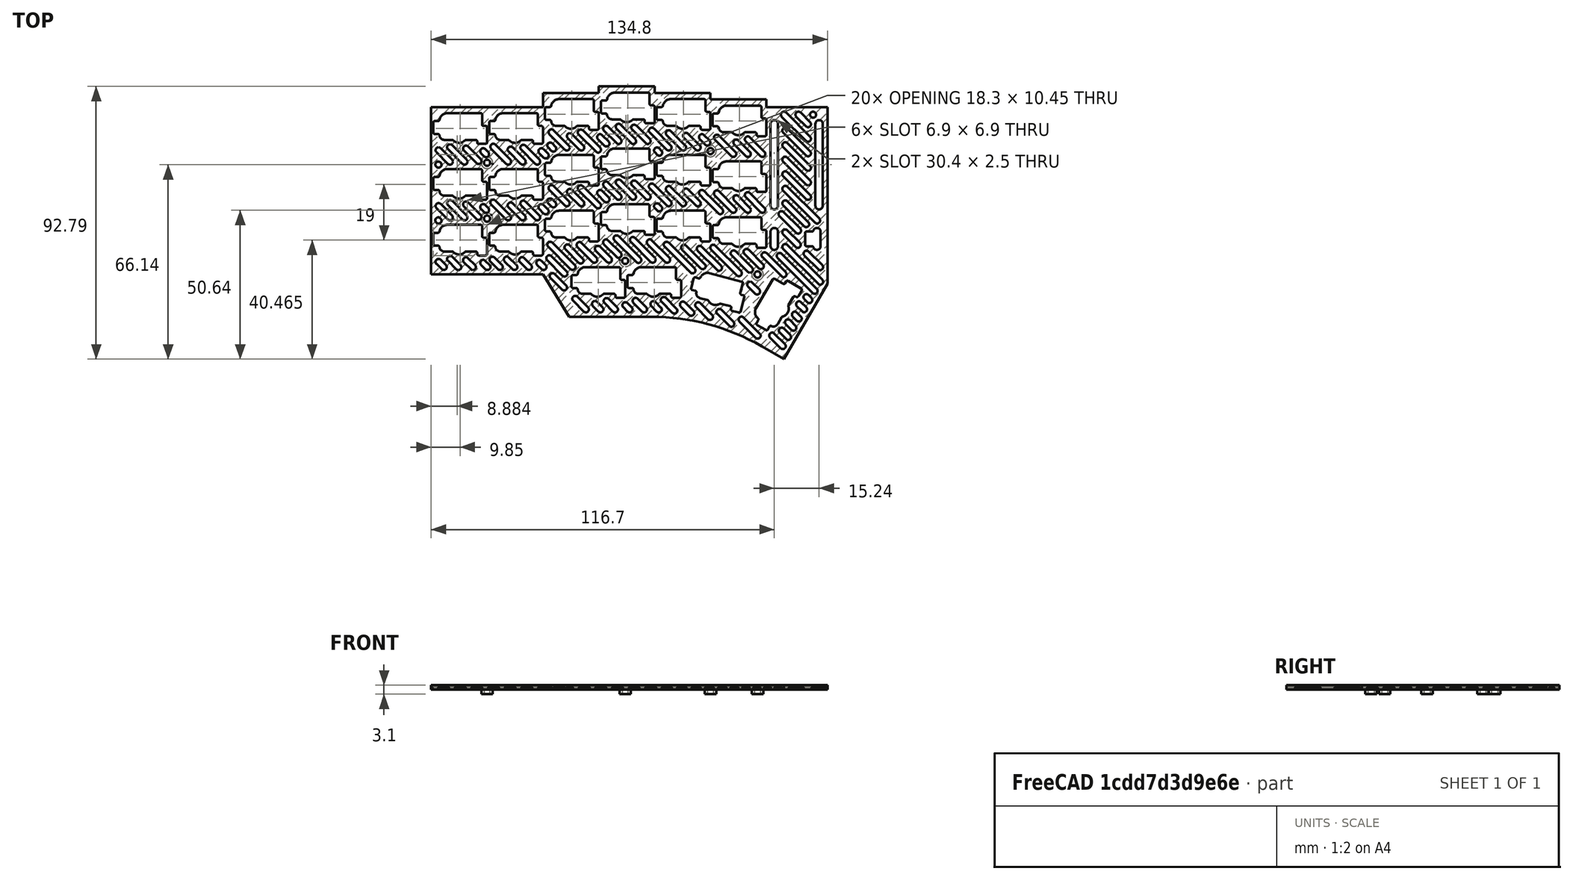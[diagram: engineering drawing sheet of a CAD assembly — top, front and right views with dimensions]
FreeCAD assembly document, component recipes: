
FREECAD ASSEMBLY — COMPONENT RECIPES ("key-v3")

This assembly document has 4 components, labeled P0..P3 below (a component is one placed body or linked part). 4 of them carry a construction recipe — the FreeCAD feature program that regenerates the part from scratch, quoted from this document or its linked companion documents; the rest are supplied as boundary geometry only. No exploded tour is included for this assembly.
COMPONENT P0 — recipe-attached ("base body", modeled in this document).
Construction recipe (the document's own serialized feature program — sketch geometry with constraints, then the solid features built on it; lengths are millimeters unless a unit is written):

FEATURE [Sketcher::SketchObject] Sketch001  label="pcb contour"
  AttachmentSupport = -> [XY_Plane]
  FullyConstrained = true
  MapMode = 5
  expr: Constraints[36] = 19 * 3
  sketch-geometry (39):
    g0: LineSegment StartX=-9.5 StartY=9.5 StartZ=0 EndX=28.5 EndY=9.5 EndZ=0
    g1: LineSegment StartX=28.5 StartY=9.5 StartZ=0 EndX=28.5 EndY=14.3 EndZ=0
    g2: LineSegment StartX=28.5 StartY=14.3 StartZ=0 EndX=47.5 EndY=14.3 EndZ=0
    g3: LineSegment StartX=47.5 StartY=14.3 StartZ=0 EndX=47.5 EndY=16.5 EndZ=0
    g4: LineSegment StartX=47.5 StartY=16.5 StartZ=0 EndX=66.5 EndY=16.5 EndZ=0
    g5: LineSegment StartX=66.5 StartY=16.5 StartZ=0 EndX=66.5 EndY=14.3 EndZ=0
    g6: LineSegment StartX=66.5 StartY=14.3 StartZ=0 EndX=85.5 EndY=14.3 EndZ=0
    g7: LineSegment StartX=85.5 StartY=14.3 StartZ=0 EndX=85.5 EndY=12.1 EndZ=0
    g8: LineSegment StartX=85.5 StartY=12.1 StartZ=0 EndX=104.5 EndY=12.1 EndZ=0
    g9: LineSegment StartX=104.5 StartY=12.1 StartZ=0 EndX=104.5 EndY=9.4 EndZ=0
    g10: LineSegment StartX=104.5 StartY=9.4 StartZ=0 EndX=125.3 EndY=9.4 EndZ=0
    g11: LineSegment StartX=-9.5 StartY=9.5 StartZ=0 EndX=-9.5 EndY=-47.5 EndZ=0
    g12: LineSegment StartX=-9.5 StartY=-47.5 StartZ=0 EndX=28.5 EndY=-47.5 EndZ=0
    g13: LineSegment StartX=28.5 StartY=-47.5 StartZ=0 EndX=37.45 EndY=-61.9 EndZ=0
    g14: LineSegment StartX=37.45 StartY=-61.9 StartZ=0 EndX=56.45 EndY=-61.9 EndZ=0
    g15: LineSegment StartX=56.45 StartY=-61.9 StartZ=0 EndX=56.45 EndY=-42.9 EndZ=0
    g16: LineSegment StartX=56.45 StartY=-42.9 StartZ=0 EndX=37.45 EndY=-42.9 EndZ=0
    g17: LineSegment StartX=37.45 StartY=-42.9 StartZ=0 EndX=37.45 EndY=-61.9 EndZ=0
    g18: LineSegment StartX=56.45 StartY=-61.9 StartZ=0 EndX=75.45 EndY=-61.9 EndZ=0
    g19: LineSegment StartX=75.45 StartY=-61.9 StartZ=0 EndX=75.45 EndY=-42.9 EndZ=0
    g20: LineSegment StartX=75.45 StartY=-42.9 StartZ=0 EndX=56.45 EndY=-42.9 EndZ=0
    g21: LineSegment StartX=56.45 StartY=-42.9 StartZ=0 EndX=56.45 EndY=-61.9 EndZ=0
    g22: GeomPoint X=65.95 Y=-52.4 Z=0
    g23: LineSegment StartX=110.452 StartY=-76.2909 StartZ=0 EndX=93.9978 EndY=-66.7909 EndZ=0
    g24: LineSegment StartX=93.9978 StartY=-66.7909 StartZ=0 EndX=108.248 EndY=-42.1091 EndZ=0
    g25: LineSegment StartX=108.248 StartY=-42.1091 StartZ=0 EndX=124.702 EndY=-51.6091 EndZ=0
    g26: LineSegment StartX=124.702 StartY=-51.6091 StartZ=0 EndX=110.452 EndY=-76.2909 EndZ=0
    g27: GeomPoint X=109.35 Y=-59.2 Z=0
    g28: LineSegment StartX=75.5149 StartY=-61.9175 StartZ=0 EndX=80.4325 EndY=-43.5649 EndZ=0
    g29: LineSegment StartX=80.4325 StartY=-43.5649 StartZ=0 EndX=98.7851 EndY=-48.4825 EndZ=0
    g30: LineSegment StartX=98.7851 StartY=-48.4825 StartZ=0 EndX=93.8675 EndY=-66.8351 EndZ=0
    g31: LineSegment StartX=93.8675 StartY=-66.8351 StartZ=0 EndX=75.5149 EndY=-61.9175 EndZ=0
    g32: GeomPoint X=87.15 Y=-55.2 Z=0
    g33: LineSegment StartX=37.45 StartY=-61.9 StartZ=0 EndX=65.4303 EndY=-61.9 EndZ=0
    g34: LineSegment StartX=110.452 StartY=-76.2909 StartZ=0 EndX=102.93 EndY=-71.9481 EndZ=0
    g35: LineSegment StartX=125.3 StartY=9.4 StartZ=0 EndX=125.3 EndY=-50.5738 EndZ=0
    g36: LineSegment StartX=110.452 StartY=-76.2909 StartZ=0 EndX=125.3 EndY=-50.5738 EndZ=0
    g37: ArcOfCircle CenterX=65.4303 CenterY=-136.9 CenterZ=0 NormalX=0 NormalY=0 NormalZ=1 AngleXU=0 Radius=75 StartAngle=1.0472 EndAngle=1.5708
    g38: GeomPoint X=85.5265 Y=-61.9 Z=0
  constraints (105):
    c: Horizontal(g0)
    c: Coincident(g1,g0)
    c: Vertical(g1)
    c: Coincident(g2,g1)
    c: Horizontal(g2)
    c: Coincident(g3,g2)
    c: Vertical(g3)
    c: Coincident(g4,g3)
    c: Horizontal(g4)
    c: Coincident(g5,g4)
    c: Vertical(g5)
    c: Coincident(g6,g5)
    c: Horizontal(g6)
    c: Coincident(g7,g6)
    c: Vertical(g7)
    c: Coincident(g8,g7)
    c: Horizontal(g8)
    c: Coincident(g9,g8)
    c: Vertical(g9)
    c: Coincident(g10,g9)
    c: Horizontal(g10)
    c: DistanceX(g0,g-1) = 9.5
    c: Distance(g-1,g0) = 9.5
    c: DistanceX(g0,g0) = 38
    c: DistanceX(g2,g2) = 19
    c: Equal(g4,g2)
    c: Equal(g2,g6)
    c: Equal(g6,g8)
    c: DistanceY(g1,g1) = 4.8
    c: DistanceY(g3,g3) = 2.2
    c: DistanceY(g5,g5) = 2.2
    c: DistanceY(g7,g7) = 2.2
    c: DistanceY(g9,g9) = 2.7
    c: DistanceX(g10,g10) = 20.8
    c: Coincident(g11,g0)
    c: Vertical(g11)
    c: DistanceY(g11,g11) = 57
    c: Coincident(g12,g11)
    c: Horizontal(g12)
    c: DistanceX(g12,g12) = 38
    c: Coincident(g13,g12)
    c: DistanceX(g12,g13) = 8.95
    c: DistanceY(g13,g12) = 14.4
    c: Coincident(g14,g15)
    c: Coincident(g15,g16)
    c: Coincident(g16,g17)
    c: Coincident(g17,g14)
    c: Horizontal(g14)
    c: Horizontal(g16)
    c: Vertical(g15)
    c: Vertical(g17)
    c: Coincident(g14,g13)
    c: Equal(g17,g16)
    c: DistanceX(g16,g16) = 19
    c: Coincident(g18,g19)
    c: Coincident(g19,g20)
    c: Coincident(g20,g21)
    c: Coincident(g21,g18)
    c: Horizontal(g18)
    c: Horizontal(g20)
    c: Vertical(g19)
    c: Vertical(g21)
    c: Coincident(g18,g14)
    c: Equal(g20,g19)
    c: Equal(g19,g16)
    c: Symmetric(g14,g19,g22)
    c: Coincident(g24,g23)
    c: Coincident(g25,g24)
    c: Coincident(g26,g25)
    c: Coincident(g26,g23)
    c: Parallel(g25,g23)
    c: Parallel(g24,g26)
    c: Perpendicular(g25,g24)
    c: Equal(g23,g19)
    c: Symmetric(g25,g23,g27)
    c: Coincident(g29,g28)
    c: Coincident(g30,g29)
    c: Coincident(g31,g30)
    c: Coincident(g31,g28)
    c: Parallel(g30,g28)
    c: Parallel(g29,g31)
    c: Perpendicular(g30,g29)
    c: Equal(g29,g28)
    c: Symmetric(g30,g28,g32)
    c: Angle(g31,g18) = 0.261799
    c: Angle(g18,g26) = 1.0472
    c: DistanceX(g22,g32) = 21.2
    c: DistanceY(g32,g22) = 2.8
    c: Equal(g28,g19)
    c: DistanceX(g32,g27) = 22.2
    c: DistanceY(g27,g32) = 4
    c: Distance(g26,g26) = 28.5
    c: Coincident(g33,g13)
    c: Horizontal(g33)
    c: Tangent(g34,g23) = -1.5708
    c: Coincident(g35,g10)
    c: Vertical(g35)
    c: Coincident(g36,g23)
    c: Tangent(g26,g36)
    c: Coincident(g36,g35)
    c: PointOnObject(g38,g34)
    c: PointOnObject(g38,g33)
    c: Tangent(g34,g37) = -1.5708
    c: Tangent(g33,g37) = 1.5708
    c: Radius(g37) = 75
FEATURE [PartDesign::Pad] Pad  label="base"
  Direction = (0,0,1)
  Length = 1.5
  Length2 = 10
  Profile = -> Sketch001
  ReferenceAxis = -> Sketch001 [N_Axis]
  Suppressed = false
  Type = 0
  expr: Length = <<constants>>.base_normal
FEATURE [PartDesign::Body] Body  label="base body"
  Group = -> [Sketch001,Pad]
  Origin = -> Origin
  Tip = -> Pad
COMPONENT P1 — recipe-attached ("Body003", modeled in this document).
Construction recipe (the document's own serialized feature program — sketch geometry with constraints, then the solid features built on it; lengths are millimeters unless a unit is written):

FEATURE [PartDesign::FeatureBase] BaseFeature
  BaseFeature = -> Cut002
  Suppressed = false
FEATURE [PartDesign::Plane] DatumPlane
  AttachmentSupport = -> [BaseFeature,Z_Axis003]
  Length = 196.764
  MapMode = 13
  Placement = pos=(-6.33333,6.33333,0.5) rot=(0.281085,0.678598,0.678598;2.59356rad)
  ResizeMode = 0
  Width = 68.8627
FEATURE [Sketcher::SketchObject] Sketch003
  AttachmentSupport = -> [DatumPlane]
  ExternalGeometry = -> [BaseFeature]
  FullyConstrained = true
  MapMode = 5
  Placement = pos=(-6.33333,6.33333,0.5) rot=(0.281085,0.678598,0.678598;2.59356rad)
  expr: Constraints[6] = <<constants>>.slot_height
  expr: Constraints[9] = <<constants>>.base_thin
  sketch-geometry (4):
    g0: ArcOfCircle CenterX=2.17834 CenterY=0.1 CenterZ=0 NormalX=0 NormalY=0 NormalZ=1 AngleXU=0 Radius=0.3 StartAngle=4.71239 EndAngle=7.85398
    g1: ArcOfCircle CenterX=0.178343 CenterY=0.1 CenterZ=0 NormalX=0 NormalY=0 NormalZ=1 AngleXU=0 Radius=0.3 StartAngle=1.5708 EndAngle=4.71239
    g2: LineSegment StartX=2.17834 StartY=-0.2 StartZ=0 EndX=0.178343 EndY=-0.2 EndZ=0
    g3: LineSegment StartX=2.17834 StartY=0.4 StartZ=0 EndX=0.178343 EndY=0.4 EndZ=0
  constraints (10):
    c: Tangent(g0,g2) = 1.5708
    c: Tangent(g0,g3) = -1.5708
    c: Tangent(g1,g2) = 1.5708
    c: Tangent(g1,g3) = -1.5708
    c: Equal(g0,g1)
    c: Horizontal(g2)
    c: Distance(g3,g2) = 0.6
    c: DistanceX(g1,g0) = 2
    c: Distance(g0,g-4) = 2
    c: Distance(g-5,g2) = 0.3
FEATURE [PartDesign::Pocket] Pocket
  BaseFeature = -> BaseFeature
  Direction = (-0.707107,-0.707107,0)
  Length = 5
  Length2 = 5
  Midplane = true
  Profile = -> Sketch003
  ReferenceAxis = -> Sketch003 [N_Axis]
  Suppressed = false
  Type = 1
FEATURE [PartDesign::LinearPattern] LinearPattern
  BaseFeature = -> Pocket
  Direction = -> Sketch003 [H_Axis]
  Length = 156
  Mode = 1
  Occurrences = 40
  Offset = 4
  Originals = -> [Pocket]
  Reversed = true
  Suppressed = false
FEATURE [Sketcher::SketchObject] Sketch004
  AttachmentSupport = -> [LinearPattern]
  FullyConstrained = true
  MapMode = 5
  Placement = pos=(0,0,0) rot=(1,0,0;3.14159rad)
  expr: Constraints[5] = 9.5 + 19
  sketch-geometry (5):
    g0: Circle CenterX=9.5 CenterY=9.5 CenterZ=0 NormalX=0 NormalY=0 NormalZ=1 AngleXU=0 Radius=1.95
    g1: Circle CenterX=9.5 CenterY=28.5 CenterZ=0 NormalX=0 NormalY=0 NormalZ=1 AngleXU=0 Radius=1.95
    g2: Circle CenterX=56.5 CenterY=42.9 CenterZ=0 NormalX=0 NormalY=0 NormalZ=1 AngleXU=0 Radius=1.95
    g3: Circle CenterX=85.5 CenterY=5.5 CenterZ=0 NormalX=0 NormalY=0 NormalZ=1 AngleXU=0 Radius=1.95
    g4: Circle CenterX=101.5 CenterY=47.5 CenterZ=0 NormalX=0 NormalY=0 NormalZ=1 AngleXU=0 Radius=1.95
  constraints (15):
    c: Diameter(g0) = 3.9
    c: DistanceY(g-1,g0) = 9.5
    c: DistanceX(g-1,g0) = 9.5
    c: Equal(g1,g0)
    c: Distance(g1,g-2) = 9.5
    c: Distance(g1,g-1) = 28.5
    c: DistanceX(g-1,g2) = 56.5
    c: DistanceY(g-1,g2) = 42.9
    c: Equal(g2,g3)
    c: Equal(g3,g1)
    c: DistanceX(g-1,g3) = 85.5
    c: DistanceY(g-1,g3) = 5.5
    c: DistanceX(g-1,g4) = 101.5
    c: DistanceY(g-1,g4) = 47.5
    c: Equal(g4,g0)
FEATURE [PartDesign::Pad] Pad002
  BaseFeature = -> LinearPattern
  Direction = (0,0,-1)
  Length = 1.6
  Length2 = 10
  Profile = -> Sketch004
  ReferenceAxis = -> Sketch004 [N_Axis]
  Suppressed = false
  Type = 0
FEATURE [Sketcher::SketchObject] Sketch005
  AttachmentSupport = -> [Pad002]
  ExternalGeometry = -> [Pad002]
  FullyConstrained = true
  MapMode = 5
  Placement = pos=(0,0,0) rot=(1,0,0;3.14159rad)
  sketch-geometry (100):
    g0: ArcOfCircle CenterX=-7 CenterY=5.21569 CenterZ=0 NormalX=0 NormalY=0 NormalZ=1 AngleXU=0 Radius=1 StartAngle=2.35619 EndAngle=5.49779
    g1: ArcOfCircle CenterX=-3.11569 CenterY=9.1 CenterZ=0 NormalX=0 NormalY=0 NormalZ=1 AngleXU=0 Radius=1 StartAngle=5.49779 EndAngle=8.63938
    g2: LineSegment StartX=-7.70711 StartY=5.9228 StartZ=0 EndX=-3.8228 EndY=9.80711 EndZ=0
    g3: LineSegment StartX=-6.29289 StartY=4.50858 StartZ=0 EndX=-2.40858 EndY=8.39289 EndZ=0
    g4: ArcOfCircle CenterX=-3.06594 CenterY=4.2 CenterZ=0 NormalX=0 NormalY=0 NormalZ=1 AngleXU=0 Radius=1 StartAngle=2.35619 EndAngle=5.49779
    g5: ArcOfCircle CenterX=1.83406 CenterY=9.1 CenterZ=0 NormalX=0 NormalY=0 NormalZ=1 AngleXU=0 Radius=1 StartAngle=5.49779 EndAngle=8.63938
    g6: LineSegment StartX=-3.77305 StartY=4.90711 StartZ=0 EndX=1.12695 EndY=9.80711 EndZ=0
    g7: LineSegment StartX=-2.35884 StartY=3.49289 StartZ=0 EndX=2.54117 EndY=8.39289 EndZ=0
    g8: ArcOfCircle CenterX=2.33172 CenterY=4.64791 CenterZ=0 NormalX=0 NormalY=0 NormalZ=1 AngleXU=0 Radius=1 StartAngle=2.35619 EndAngle=5.49779
    g9: ArcOfCircle CenterX=6.60687 CenterY=8.92306 CenterZ=0 NormalX=0 NormalY=0 NormalZ=1 AngleXU=0 Radius=1 StartAngle=5.49779 EndAngle=8.63938
    g10: LineSegment StartX=1.62461 StartY=5.35502 StartZ=0 EndX=5.89976 EndY=9.63016 EndZ=0
    g11: LineSegment StartX=3.03883 StartY=3.94081 StartZ=0 EndX=7.31397 EndY=8.21595 EndZ=0
    g12: ArcOfCircle CenterX=8.18356 CenterY=5.55 CenterZ=0 NormalX=0 NormalY=0 NormalZ=1 AngleXU=0 Radius=1 StartAngle=2.35619 EndAngle=5.49779
    g13: ArcOfCircle CenterX=9.19886 CenterY=6.56531 CenterZ=0 NormalX=0 NormalY=0 NormalZ=1 AngleXU=0 Radius=1 StartAngle=5.49779 EndAngle=8.63938
    g14: LineSegment StartX=7.47645 StartY=6.25711 StartZ=0 EndX=8.49176 EndY=7.27242 EndZ=0
    g15: LineSegment StartX=8.89066 StartY=4.84289 StartZ=0 EndX=9.90597 EndY=5.8582 EndZ=0
    g16: ArcOfCircle CenterX=11.6109 CenterY=4.02759 CenterZ=0 NormalX=0 NormalY=0 NormalZ=1 AngleXU=0 Radius=1 StartAngle=2.35619 EndAngle=5.49779
    g17: ArcOfCircle CenterX=16.6833 CenterY=9.1 CenterZ=0 NormalX=0 NormalY=0 NormalZ=1 AngleXU=0 Radius=1 StartAngle=5.49779 EndAngle=8.63938
    g18: LineSegment StartX=10.9038 StartY=4.73469 StartZ=0 EndX=15.9762 EndY=9.80711 EndZ=0
    g19: LineSegment StartX=12.318 StartY=3.32048 StartZ=0 EndX=17.3904 EndY=8.39289 EndZ=0
    g20: ArcOfCircle CenterX=17.5171 CenterY=4.98409 CenterZ=0 NormalX=0 NormalY=0 NormalZ=1 AngleXU=0 Radius=1 StartAngle=2.35619 EndAngle=5.49779
    g21: ArcOfCircle CenterX=21.6331 CenterY=9.1 CenterZ=0 NormalX=0 NormalY=0 NormalZ=1 AngleXU=0 Radius=1 StartAngle=5.49779 EndAngle=8.63938
    g22: LineSegment StartX=16.81 StartY=5.69119 StartZ=0 EndX=20.9259 EndY=9.80711 EndZ=0
    g23: LineSegment StartX=18.2242 StartY=4.27698 StartZ=0 EndX=22.3402 EndY=8.39289 EndZ=0
    g24: ArcOfCircle CenterX=21.8392 CenterY=4.35645 CenterZ=0 NormalX=0 NormalY=0 NormalZ=1 AngleXU=0 Radius=1 StartAngle=2.35619 EndAngle=5.49779
    g25: ArcOfCircle CenterX=26.5828 CenterY=9.1 CenterZ=0 NormalX=0 NormalY=0 NormalZ=1 AngleXU=0 Radius=1 StartAngle=5.49779 EndAngle=8.63938
    g26: LineSegment StartX=21.1321 StartY=5.06356 StartZ=0 EndX=25.8757 EndY=9.80711 EndZ=0
    g27: LineSegment StartX=22.5464 StartY=3.64934 StartZ=0 EndX=27.2899 EndY=8.39289 EndZ=0
    g28: ArcOfCircle CenterX=27.9825 CenterY=5.55 CenterZ=0 NormalX=0 NormalY=0 NormalZ=1 AngleXU=0 Radius=1 StartAngle=2.35619 EndAngle=5.49779
    g29: ArcOfCircle CenterX=29.4376 CenterY=7.00507 CenterZ=0 NormalX=0 NormalY=0 NormalZ=1 AngleXU=0 Radius=1 StartAngle=5.49779 EndAngle=8.63938
    g30: LineSegment StartX=27.2754 StartY=6.25711 StartZ=0 EndX=28.7305 EndY=7.71218 EndZ=0
    g31: LineSegment StartX=28.6897 StartY=4.84289 StartZ=0 EndX=30.1447 EndY=6.29796 EndZ=0
    g32: ArcOfCircle CenterX=31 CenterY=3.6177 CenterZ=0 NormalX=0 NormalY=0 NormalZ=1 AngleXU=0 Radius=1 StartAngle=2.35619 EndAngle=5.49779
    g33: ArcOfCircle CenterX=32.0584 CenterY=4.67609 CenterZ=0 NormalX=0 NormalY=0 NormalZ=1 AngleXU=0 Radius=1 StartAngle=5.49779 EndAngle=8.63938
    g34: LineSegment StartX=30.2929 StartY=4.32481 StartZ=0 EndX=31.3513 EndY=5.38319 EndZ=0
    g35: LineSegment StartX=31.7071 StartY=2.9106 StartZ=0 EndX=32.7655 EndY=3.96898 EndZ=0
    g36: ArcOfCircle CenterX=31.4259 CenterY=-0.906125 CenterZ=0 NormalX=0 NormalY=0 NormalZ=1 AngleXU=0 Radius=1 StartAngle=2.35619 EndAngle=5.49779
    g37: ArcOfCircle CenterX=36.632 CenterY=4.3 CenterZ=0 NormalX=0 NormalY=0 NormalZ=1 AngleXU=0 Radius=1 StartAngle=5.49779 EndAngle=8.63938
    g38: LineSegment StartX=30.7188 StartY=-0.199018 StartZ=0 EndX=35.9249 EndY=5.00711 EndZ=0
    g39: LineSegment StartX=32.133 StartY=-1.61323 StartZ=0 EndX=37.3392 EndY=3.59289 EndZ=0
    g40: ArcOfCircle CenterX=37.6714 CenterY=0.389607 CenterZ=0 NormalX=0 NormalY=0 NormalZ=1 AngleXU=0 Radius=1 StartAngle=2.35619 EndAngle=5.49779
    g41: ArcOfCircle CenterX=41.5818 CenterY=4.3 CenterZ=0 NormalX=0 NormalY=0 NormalZ=1 AngleXU=0 Radius=1 StartAngle=5.49779 EndAngle=8.63938
    g42: LineSegment StartX=36.9643 StartY=1.09671 StartZ=0 EndX=40.8747 EndY=5.00711 EndZ=0
    g43: LineSegment StartX=38.3785 StartY=-0.3175 StartZ=0 EndX=42.2889 EndY=3.59289 EndZ=0
    g44: ArcOfCircle CenterX=41.3817 CenterY=-0.849816 CenterZ=0 NormalX=0 NormalY=0 NormalZ=1 AngleXU=0 Radius=1 StartAngle=2.35619 EndAngle=5.49779
    g45: ArcOfCircle CenterX=47.2624 CenterY=5.03088 CenterZ=0 NormalX=0 NormalY=0 NormalZ=1 AngleXU=0 Radius=1 StartAngle=5.49779 EndAngle=8.63938
    g46: LineSegment StartX=40.6746 StartY=-0.142709 StartZ=0 EndX=46.5553 EndY=5.73799 EndZ=0
    g47: LineSegment StartX=42.0888 StartY=-1.55692 StartZ=0 EndX=47.9695 EndY=4.32378 EndZ=0
    g48: ArcOfCircle CenterX=47.9313 CenterY=0.75 CenterZ=0 NormalX=0 NormalY=0 NormalZ=1 AngleXU=0 Radius=1 StartAngle=2.35619 EndAngle=5.49779
    g49: ArcOfCircle CenterX=50.1391 CenterY=2.95777 CenterZ=0 NormalX=0 NormalY=0 NormalZ=1 AngleXU=0 Radius=1 StartAngle=5.49779 EndAngle=8.63938
    g50: LineSegment StartX=47.2242 StartY=1.45711 StartZ=0 EndX=49.4319 EndY=3.66487 EndZ=0
    g51: LineSegment StartX=48.6384 StartY=0.0428931 StartZ=0 EndX=50.8462 EndY=2.25066 EndZ=0
    g52: ArcOfCircle CenterX=50 CenterY=-2.13104 CenterZ=0 NormalX=0 NormalY=0 NormalZ=1 AngleXU=0 Radius=1 StartAngle=2.35619 EndAngle=5.49779
    g53: ArcOfCircle CenterX=54.231 CenterY=2.1 CenterZ=0 NormalX=0 NormalY=0 NormalZ=1 AngleXU=0 Radius=1 StartAngle=5.49779 EndAngle=8.63938
    g54: LineSegment StartX=49.2929 StartY=-1.42393 StartZ=0 EndX=53.5239 EndY=2.80711 EndZ=0
    g55: LineSegment StartX=50.7071 StartY=-2.83814 StartZ=0 EndX=54.9381 EndY=1.39289 EndZ=0
    g56: ArcOfCircle CenterX=54.2808 CenterY=-2.8 CenterZ=0 NormalX=0 NormalY=0 NormalZ=1 AngleXU=0 Radius=1 StartAngle=2.35619 EndAngle=5.49779
    g57: ArcOfCircle CenterX=59.1808 CenterY=2.1 CenterZ=0 NormalX=0 NormalY=0 NormalZ=1 AngleXU=0 Radius=1 StartAngle=5.49779 EndAngle=8.63938
    g58: LineSegment StartX=53.5737 StartY=-2.09289 StartZ=0 EndX=58.4737 EndY=2.80711 EndZ=0
    g59: LineSegment StartX=54.9879 StartY=-3.50711 StartZ=0 EndX=59.8879 EndY=1.39289 EndZ=0
    g60: ArcOfCircle CenterX=59.5579 CenterY=-2.47263 CenterZ=0 NormalX=0 NormalY=0 NormalZ=1 AngleXU=0 Radius=1 StartAngle=2.35619 EndAngle=5.49779
    g61: ArcOfCircle CenterX=64.1305 CenterY=2.1 CenterZ=0 NormalX=0 NormalY=0 NormalZ=1 AngleXU=0 Radius=1 StartAngle=5.49779 EndAngle=8.63938
    g62: LineSegment StartX=58.8508 StartY=-1.76552 StartZ=0 EndX=63.4234 EndY=2.80711 EndZ=0
    g63: LineSegment StartX=60.265 StartY=-3.17973 StartZ=0 EndX=64.8376 EndY=1.39289 EndZ=0
    g64: ArcOfCircle CenterX=65.5303 CenterY=-1.45 CenterZ=0 NormalX=0 NormalY=0 NormalZ=1 AngleXU=0 Radius=1 StartAngle=2.35619 EndAngle=5.49779
    g65: ArcOfCircle CenterX=71.2803 CenterY=4.3 CenterZ=0 NormalX=0 NormalY=0 NormalZ=1 AngleXU=0 Radius=1 StartAngle=5.49779 EndAngle=8.63938
    g66: LineSegment StartX=64.8232 StartY=-0.742893 StartZ=0 EndX=70.5732 EndY=5.00711 EndZ=0
    g67: LineSegment StartX=66.2374 StartY=-2.15711 StartZ=0 EndX=71.9874 EndY=3.59289 EndZ=0
    g68: ArcOfCircle CenterX=67.3 CenterY=5.26947 CenterZ=0 NormalX=0 NormalY=0 NormalZ=1 AngleXU=0 Radius=1 StartAngle=2.35619 EndAngle=5.49779
    g69: ArcOfCircle CenterX=68.0958 CenterY=6.06528 CenterZ=0 NormalX=0 NormalY=0 NormalZ=1 AngleXU=0 Radius=1 StartAngle=5.49779 EndAngle=8.63938
    g70: LineSegment StartX=66.5929 StartY=5.97657 StartZ=0 EndX=67.3887 EndY=6.77238 EndZ=0
    g71: LineSegment StartX=68.0071 StartY=4.56236 StartZ=0 EndX=68.8029 EndY=5.35817 EndZ=0
    g72: ArcOfCircle CenterX=71.33 CenterY=-0.6 CenterZ=0 NormalX=0 NormalY=0 NormalZ=1 AngleXU=0 Radius=1 StartAngle=2.35619 EndAngle=5.49779
    g73: ArcOfCircle CenterX=76.23 CenterY=4.3 CenterZ=0 NormalX=0 NormalY=0 NormalZ=1 AngleXU=0 Radius=1 StartAngle=5.49779 EndAngle=8.63938
    g74: LineSegment StartX=70.6229 StartY=0.107107 StartZ=0 EndX=75.5229 EndY=5.00711 EndZ=0
    g75: LineSegment StartX=72.0371 StartY=-1.30711 StartZ=0 EndX=76.9371 EndY=3.59289 EndZ=0
    g76: ArcOfCircle CenterX=77.1508 CenterY=0.271054 CenterZ=0 NormalX=0 NormalY=0 NormalZ=1 AngleXU=0 Radius=1 StartAngle=2.35619 EndAngle=5.49779
    g77: ArcOfCircle CenterX=81.1798 CenterY=4.3 CenterZ=0 NormalX=0 NormalY=0 NormalZ=1 AngleXU=0 Radius=1 StartAngle=5.49779 EndAngle=8.63938
    g78: LineSegment StartX=76.4437 StartY=0.978161 StartZ=0 EndX=80.4727 EndY=5.00711 EndZ=0
    g79: LineSegment StartX=77.8579 StartY=-0.436053 StartZ=0 EndX=81.8869 EndY=3.59289 EndZ=0
    g80: ArcOfCircle CenterX=82.5795 CenterY=0.75 CenterZ=0 NormalX=0 NormalY=0 NormalZ=1 AngleXU=0 Radius=1 StartAngle=2.35619 EndAngle=5.49779
    g81: ArcOfCircle CenterX=84.4617 CenterY=2.63217 CenterZ=0 NormalX=0 NormalY=0 NormalZ=1 AngleXU=0 Radius=1 StartAngle=5.49779 EndAngle=8.63938
    g82: LineSegment StartX=81.8724 StartY=1.45711 StartZ=0 EndX=83.7546 EndY=3.33928 EndZ=0
    g83: LineSegment StartX=83.2866 StartY=0.0428931 StartZ=0 EndX=85.1688 EndY=1.92507 EndZ=0
    g84: ArcOfCircle CenterX=87.6811 CenterY=0.901792 CenterZ=0 NormalX=0 NormalY=0 NormalZ=1 AngleXU=0 Radius=1 StartAngle=2.35619 EndAngle=5.49779
    g85: ArcOfCircle CenterX=93.2793 CenterY=6.5 CenterZ=0 NormalX=0 NormalY=0 NormalZ=1 AngleXU=0 Radius=1 StartAngle=5.49779 EndAngle=8.63938
    g86: LineSegment StartX=86.974 StartY=1.6089 StartZ=0 EndX=92.5722 EndY=7.20711 EndZ=0
    g87: LineSegment StartX=88.3882 StartY=0.194685 StartZ=0 EndX=93.9864 EndY=5.79289 EndZ=0
    g88: ArcOfCircle CenterX=94.2788 CenterY=2.54974 CenterZ=0 NormalX=0 NormalY=0 NormalZ=1 AngleXU=0 Radius=1 StartAngle=2.35619 EndAngle=5.49779
    g89: ArcOfCircle CenterX=98.229 CenterY=6.5 CenterZ=0 NormalX=0 NormalY=0 NormalZ=1 AngleXU=0 Radius=1 StartAngle=5.49779 EndAngle=8.63938
    g90: LineSegment StartX=93.5717 StartY=3.25685 StartZ=0 EndX=97.5219 EndY=7.20711 EndZ=0
    g91: LineSegment StartX=94.9859 StartY=1.84263 StartZ=0 EndX=98.9361 EndY=5.79289 EndZ=0
    g92: ArcOfCircle CenterX=98.1874 CenterY=1.5086 CenterZ=0 NormalX=0 NormalY=0 NormalZ=1 AngleXU=0 Radius=1 StartAngle=2.35619 EndAngle=5.49779
    g93: ArcOfCircle CenterX=103.179 CenterY=6.5 CenterZ=0 NormalX=0 NormalY=0 NormalZ=1 AngleXU=0 Radius=1 StartAngle=5.49779 EndAngle=8.63938
    g94: LineSegment StartX=97.4803 StartY=2.21571 StartZ=0 EndX=102.472 EndY=7.20711 EndZ=0
    g95: LineSegment StartX=98.8945 StartY=0.801498 StartZ=0 EndX=103.886 EndY=5.79289 EndZ=0
    g96: ArcOfCircle CenterX=-7.1 CenterY=10.0654 CenterZ=0 NormalX=0 NormalY=0 NormalZ=1 AngleXU=0 Radius=1 StartAngle=2.35619 EndAngle=5.49779
    g97: ArcOfCircle CenterX=-6.99407 CenterY=10.1714 CenterZ=0 NormalX=0 NormalY=0 NormalZ=1 AngleXU=0 Radius=1 StartAngle=5.49779 EndAngle=8.63938
    g98: LineSegment StartX=-7.80711 StartY=10.7725 StartZ=0 EndX=-7.70117 EndY=10.8785 EndZ=0
    g99: LineSegment StartX=-6.39289 StartY=9.35833 StartZ=0 EndX=-6.28696 EndY=9.46426 EndZ=0
  constraints (251):
    c: Tangent(g0,g2) = 1.5708
    c: Tangent(g0,g3) = -1.5708
    c: Tangent(g1,g2) = 1.5708
    c: Tangent(g1,g3) = -1.5708
    c: Equal(g0,g1)
    c: Angle(g-1,g2) = 0.785398
    c: Radius(g0) = 1
    c: Tangent(g4,g6) = 1.5708
    c: Tangent(g4,g7) = -1.5708
    c: Tangent(g5,g6) = 1.5708
    c: Tangent(g5,g7) = -1.5708
    c: Equal(g4,g5)
    c: Angle(g-1,g6) = 0.785398
    c: Radius(g4) = 1
    c: Distance(g6,g3) = 1.5
    c: Distance(g1,g-3) = 1.5
    c: Distance(g5,g-3) = 1.5
    c: Distance(g4,g-4) = 1.5
    c: Distance(g4,g-5) = 1.5
    c: Distance(g0,g-6) = 1.5
    c: Tangent(g8,g10) = 1.5708
    c: Tangent(g8,g11) = -1.5708
    c: Tangent(g9,g10) = 1.5708
    c: Tangent(g9,g11) = -1.5708
    c: Equal(g8,g9)
    c: Angle(g-1,g10) = 0.785398
    c: Radius(g8) = 1
    c: Tangent(g12,g14) = 1.5708
    c: Tangent(g12,g15) = -1.5708
    c: Tangent(g13,g14) = 1.5708
    c: Tangent(g13,g15) = -1.5708
    c: Equal(g12,g13)
    c: Angle(g-1,g14) = 0.785398
    c: Radius(g12) = 1
    c: Tangent(g16,g18) = 1.5708
    c: Tangent(g16,g19) = -1.5708
    c: Tangent(g17,g18) = 1.5708
    c: Tangent(g17,g19) = -1.5708
    c: Equal(g16,g17)
    c: Angle(g-1,g18) = 0.785398
    c: Radius(g16) = 1
    c: Distance(g7,g10) = 1.5
    c: Distance(g8,g-5) = 1.5
    c: Distance(g11,g14) = 1.5
    c: Distance(g18,g15) = 1.5
    c: Distance(g9,g-7) = 0.0001
    c: Distance(g13,g-7) = 0.0001
    c: Distance(g12,g-8) = 1.5
    c: Radius(g-9) = 0.5
    c: Distance(g16,g-9) = 1.5
    c: Distance(g17,g-10) = 1.5
    c: Tangent(g20,g22) = 1.5708
    c: Tangent(g20,g23) = -1.5708
    c: Tangent(g21,g22) = 1.5708
    c: Tangent(g21,g23) = -1.5708
    c: Equal(g20,g21)
    c: Angle(g-1,g22) = 0.785398
    c: Radius(g20) = 1
    c: Tangent(g24,g26) = 1.5708
    c: Tangent(g24,g27) = -1.5708
    c: Tangent(g25,g26) = 1.5708
    c: Tangent(g25,g27) = -1.5708
    c: Equal(g24,g25)
    c: Angle(g-1,g26) = 0.785398
    c: Radius(g24) = 1
    c: Distance(g19,g22) = 1.5
    c: Distance(g26,g23) = 1.5
    c: Distance(g21,g-10) = 1.5
    c: Distance(g24,g-12) = 1.5
    c: Distance(g25,g-10) = 1.5
    c: Distance(g-12,g20) = 1.5
    c: Tangent(g28,g30) = 1.5708
    c: Tangent(g28,g31) = -1.5708
    c: Tangent(g29,g30) = 1.5708
    c: Tangent(g29,g31) = -1.5708
    c: Equal(g28,g29)
    c: Angle(g-1,g30) = 0.785398
    c: Radius(g28) = 1
    c: Distance(g28,g-15) = 1.5
    c: Distance(g29,g-14) = 1.5
    c: Distance(g27,g30) = 1.5
    c: Tangent(g32,g34) = 1.5708
    c: Tangent(g32,g35) = -1.5708
    c: Tangent(g33,g34) = 1.5708
    c: Tangent(g33,g35) = -1.5708
    c: Equal(g32,g33)
    c: Angle(g-1,g34) = 0.785398
    c: Radius(g32) = 1
    c: Distance(g34,g31) = 1.5
    c: Distance(g-14,g33) = 1.5
    c: Distance(g32,g-16) = 1.5
    c: Tangent(g36,g38) = 1.5708
    c: Tangent(g36,g39) = -1.5708
    c: Tangent(g37,g38) = 1.5708
    c: Tangent(g37,g39) = -1.5708
    c: Equal(g36,g37)
    c: Angle(g-1,g38) = 0.785398
    c: Radius(g36) = 1
    c: Tangent(g40,g42) = 1.5708
    c: Tangent(g40,g43) = -1.5708
    c: Tangent(g41,g42) = 1.5708
    c: Tangent(g41,g43) = -1.5708
    c: Equal(g40,g41)
    c: Angle(g-1,g42) = 0.785398
    c: Radius(g40) = 1
    c: Tangent(g44,g46) = 1.5708
    c: Tangent(g44,g47) = -1.5708
    c: Tangent(g45,g46) = 1.5708
    c: Tangent(g45,g47) = -1.5708
    c: Equal(g44,g45)
    c: Angle(g-1,g46) = 0.785398
    c: Radius(g44) = 1
    c: Distance(g35,g38) = 1.5
    c: Distance(g42,g39) = 1.5
    c: Distance(g46,g43) = 1.5
    c: Tangent(g48,g50) = 1.5708
    c: Tangent(g48,g51) = -1.5708
    c: Tangent(g49,g50) = 1.5708
    c: Tangent(g49,g51) = -1.5708
    c: Equal(g48,g49)
    c: Angle(g-1,g50) = 0.785398
    c: Radius(g48) = 1
    c: Distance(g47,g50) = 1.5
    c: Tangent(g52,g54) = 1.5708
    c: Tangent(g52,g55) = -1.5708
    c: Tangent(g53,g54) = 1.5708
    c: Tangent(g53,g55) = -1.5708
    c: Equal(g52,g53)
    c: Angle(g-1,g54) = 0.785398
    c: Radius(g52) = 1
    c: Distance(g51,g54) = 1.5
    c: Distance(g37,g-17) = 1.5
    c: Distance(g41,g-17) = 1.5
    c: Distance(g-25,g45) = 1.5
    c: Distance(g36,g-21) = 1.5
    c: Distance(g40,g-18) = 1.5
    c: Distance(g44,g-18) = 1.5
    c: Distance(g48,g-19) = 1.5
    c: Distance(g49,g-22) = 1.5
    c: Distance(g52,g-20) = 1.5
    c: Distance(g53,g-24) = 1.5
    c: Tangent(g56,g58) = 1.5708
    c: Tangent(g56,g59) = -1.5708
    c: Tangent(g57,g58) = 1.5708
    c: Tangent(g57,g59) = -1.5708
    c: Equal(g56,g57)
    c: Angle(g-1,g58) = 0.785398
    c: Radius(g56) = 1
    c: Tangent(g60,g62) = 1.5708
    c: Tangent(g60,g63) = -1.5708
    c: Tangent(g61,g62) = 1.5708
    c: Tangent(g61,g63) = -1.5708
    c: Equal(g60,g61)
    c: Angle(g-1,g62) = 0.785398
    c: Radius(g60) = 1
    c: Tangent(g64,g66) = 1.5708
    c: Tangent(g64,g67) = -1.5708
    c: Tangent(g65,g66) = 1.5708
    c: Tangent(g65,g67) = -1.5708
    c: Equal(g64,g65)
    c: Angle(g-1,g66) = 0.785398
    c: Radius(g64) = 1
    c: Distance(g55,g58) = 1.5
    c: Distance(g62,g59) = 1.5
    c: Distance(g66,g63) = 1.5
    c: Distance(g56,g-26) = 1.5
    c: Distance(g60,g-27) = 1.5
    c: Distance(g57,g-24) = 1.5
    c: Distance(g61,g-24) = 1.5
    c: Distance(g64,g-28) = 1.5
    c: Distance(g65,g-31) = 1.5
    c: Tangent(g68,g70) = 1.5708
    c: Tangent(g68,g71) = -1.5708
    c: Tangent(g69,g70) = 1.5708
    c: Tangent(g69,g71) = -1.5708
    c: Equal(g68,g69)
    c: Angle(g-1,g70) = 0.785398
    c: Radius(g68) = 1
    c: Distance(g66,g71) = 1.5
    c: Distance(g-29,g69) = 1.5
    c: Distance(g68,g-32) = 1.5
    c: Tangent(g72,g74) = 1.5708
    c: Tangent(g72,g75) = -1.5708
    c: Tangent(g73,g74) = 1.5708
    c: Tangent(g73,g75) = -1.5708
    c: Equal(g72,g73)
    c: Angle(g-1,g74) = 0.785398
    c: Radius(g72) = 1
    c: Tangent(g76,g78) = 1.5708
    c: Tangent(g76,g79) = -1.5708
    c: Tangent(g77,g78) = 1.5708
    c: Tangent(g77,g79) = -1.5708
    c: Equal(g76,g77)
    c: Angle(g-1,g78) = 0.785398
    c: Radius(g76) = 1
    c: Tangent(g80,g82) = 1.5708
    c: Tangent(g80,g83) = -1.5708
    c: Tangent(g81,g82) = 1.5708
    c: Tangent(g81,g83) = -1.5708
    c: Equal(g80,g81)
    c: Angle(g-1,g82) = 0.785398
    c: Radius(g80) = 1
    c: Distance(g67,g74) = 1.5
    c: Distance(g78,g75) = 1.5
    c: Distance(g79,g82) = 1.5
    c: Distance(g72,g-33) = 1.5
    c: Distance(g73,g-31) = 1.5
    c: Distance(g77,g-31) = 1.5
    c: Distance(g76,g-34) = 1.5
    c: Distance(g80,g-35) = 1.5
    c: Distance(g81,g-36) = 0.1
    c: Tangent(g84,g86) = 1.5708
    c: Tangent(g84,g87) = -1.5708
    c: Tangent(g85,g86) = 1.5708
    c: Tangent(g85,g87) = -1.5708
    c: Equal(g84,g85)
    c: Angle(g-1,g86) = 0.785398
    c: Radius(g84) = 1
    c: Tangent(g88,g90) = 1.5708
    c: Tangent(g88,g91) = -1.5708
    c: Tangent(g89,g90) = 1.5708
    c: Tangent(g89,g91) = -1.5708
    c: Equal(g88,g89)
    c: Angle(g-1,g90) = 0.785398
    c: Radius(g88) = 1
    c: Tangent(g92,g94) = 1.5708
    c: Tangent(g92,g95) = -1.5708
    c: Tangent(g93,g94) = 1.5708
    c: Tangent(g93,g95) = -1.5708
    c: Equal(g92,g93)
    c: Angle(g-1,g94) = 0.785398
    c: Radius(g92) = 1
    c: Distance(g83,g86) = 1.5
    c: Distance(g90,g87) = 1.5
    c: Distance(g91,g94) = 1.5
    c: Distance(g84,g-40) = 1.5
    c: Distance(g88,g-38) = 1.5
    c: Distance(g85,g-37) = 1.5
    c: Distance(g89,g-37) = 1.5
    c: Distance(g93,g-37) = 1.5
    c: Distance(g92,g-38) = 1.5
    c: Tangent(g96,g98) = 1.5708
    c: Tangent(g96,g99) = -1.5708
    c: Tangent(g97,g98) = 1.5708
    c: Tangent(g97,g99) = -1.5708
    c: Equal(g96,g97)
    c: Angle(g-1,g98) = 0.785398
    c: Radius(g96) = 1
    c: Distance(g-41,g97) = 1.4
    c: Distance(g2,g99) = 1.5
    c: Distance(g96,g-6) = 1.4
FEATURE [PartDesign::Pocket] Pocket001
  BaseFeature = -> Pad002
  Direction = (0,0,1)
  Length = 5
  Length2 = 5
  Profile = -> Sketch005
  ReferenceAxis = -> Sketch005 [N_Axis]
  Suppressed = false
  Type = 0
FEATURE [PartDesign::LinearPattern] LinearPattern001
  BaseFeature = -> Pocket001
  Direction = -> Sketch005 [V_Axis]
  Length = 19
  Mode = 1
  Occurrences = 2
  Offset = 19
  Originals = -> [Pocket001]
  Suppressed = false
FEATURE [Sketcher::SketchObject] Sketch006
  AttachmentSupport = -> [LinearPattern001]
  ExternalGeometry = -> [LinearPattern001]
  FullyConstrained = true
  MapMode = 5
  Placement = pos=(0,0,0) rot=(1,0,0;3.14159rad)
  sketch-geometry (172):
    g0: ArcOfCircle CenterX=-7 CenterY=43.2157 CenterZ=0 NormalX=0 NormalY=0 NormalZ=1 AngleXU=0 Radius=1 StartAngle=2.35619 EndAngle=5.49779
    g1: ArcOfCircle CenterX=-5.21569 CenterY=45 CenterZ=0 NormalX=0 NormalY=0 NormalZ=1 AngleXU=0 Radius=1 StartAngle=5.49779 EndAngle=8.63938
    g2: LineSegment StartX=-7.70711 StartY=43.9228 StartZ=0 EndX=-5.9228 EndY=45.7071 EndZ=0
    g3: LineSegment StartX=-6.29289 StartY=42.5086 StartZ=0 EndX=-4.50858 EndY=44.2929 EndZ=0
    g4: ArcOfCircle CenterX=-3.06594 CenterY=42.2 CenterZ=0 NormalX=0 NormalY=0 NormalZ=1 AngleXU=0 Radius=1 StartAngle=2.35619 EndAngle=5.49779
    g5: ArcOfCircle CenterX=-0.265941 CenterY=45 CenterZ=0 NormalX=0 NormalY=0 NormalZ=1 AngleXU=0 Radius=1 StartAngle=5.49779 EndAngle=8.63938
    g6: LineSegment StartX=-3.77305 StartY=42.9071 StartZ=0 EndX=-0.973048 EndY=45.7071 EndZ=0
    g7: LineSegment StartX=-2.35884 StartY=41.4929 StartZ=0 EndX=0.441166 EndY=44.2929 EndZ=0
    g8: ArcOfCircle CenterX=2.33172 CenterY=42.6479 CenterZ=0 NormalX=0 NormalY=0 NormalZ=1 AngleXU=0 Radius=1 StartAngle=2.35619 EndAngle=5.49779
    g9: ArcOfCircle CenterX=4.68381 CenterY=45 CenterZ=0 NormalX=0 NormalY=0 NormalZ=1 AngleXU=0 Radius=1 StartAngle=5.49779 EndAngle=8.63938
    g10: LineSegment StartX=1.62461 StartY=43.355 StartZ=0 EndX=3.9767 EndY=45.7071 EndZ=0
    g11: LineSegment StartX=3.03883 StartY=41.9408 StartZ=0 EndX=5.39091 EndY=44.2929 EndZ=0
    g12: ArcOfCircle CenterX=8.18356 CenterY=43.55 CenterZ=0 NormalX=0 NormalY=0 NormalZ=1 AngleXU=0 Radius=1 StartAngle=2.35619 EndAngle=5.49779
    g13: ArcOfCircle CenterX=9.63356 CenterY=45 CenterZ=0 NormalX=0 NormalY=0 NormalZ=1 AngleXU=0 Radius=1 StartAngle=5.49779 EndAngle=8.63938
    g14: LineSegment StartX=7.47645 StartY=44.2571 StartZ=0 EndX=8.92645 EndY=45.7071 EndZ=0
    g15: LineSegment StartX=8.89066 StartY=42.8429 StartZ=0 EndX=10.3407 EndY=44.2929 EndZ=0
    g16: ArcOfCircle CenterX=11.3237 CenterY=42.4475 CenterZ=0 NormalX=0 NormalY=0 NormalZ=1 AngleXU=0 Radius=1 StartAngle=2.35619 EndAngle=5.49779
    g17: ArcOfCircle CenterX=13.8762 CenterY=45 CenterZ=0 NormalX=0 NormalY=0 NormalZ=1 AngleXU=0 Radius=1 StartAngle=5.49779 EndAngle=8.63938
    g18: LineSegment StartX=10.6166 StartY=43.1546 StartZ=0 EndX=13.1691 EndY=45.7071 EndZ=0
    g19: LineSegment StartX=12.0308 StartY=41.7404 StartZ=0 EndX=14.5833 EndY=44.2929 EndZ=0
    g20: ArcOfCircle CenterX=16.2212 CenterY=42.3953 CenterZ=0 NormalX=0 NormalY=0 NormalZ=1 AngleXU=0 Radius=1 StartAngle=2.35619 EndAngle=5.49779
    g21: ArcOfCircle CenterX=18.8259 CenterY=45 CenterZ=0 NormalX=0 NormalY=0 NormalZ=1 AngleXU=0 Radius=1 StartAngle=5.49779 EndAngle=8.63938
    g22: LineSegment StartX=15.5141 StartY=43.1024 StartZ=0 EndX=18.1188 EndY=45.7071 EndZ=0
    g23: LineSegment StartX=16.9283 StartY=41.6881 StartZ=0 EndX=19.5331 EndY=44.2929 EndZ=0
    g24: ArcOfCircle CenterX=21.3926 CenterY=42.6169 CenterZ=0 NormalX=0 NormalY=0 NormalZ=1 AngleXU=0 Radius=1 StartAngle=2.35619 EndAngle=5.49779
    g25: ArcOfCircle CenterX=23.7757 CenterY=45 CenterZ=0 NormalX=0 NormalY=0 NormalZ=1 AngleXU=0 Radius=1 StartAngle=5.49779 EndAngle=8.63938
    g26: LineSegment StartX=20.6855 StartY=43.324 StartZ=0 EndX=23.0686 EndY=45.7071 EndZ=0
    g27: LineSegment StartX=22.0997 StartY=41.9098 StartZ=0 EndX=24.4828 EndY=44.2929 EndZ=0
    g28: ArcOfCircle CenterX=27.2754 CenterY=43.55 CenterZ=0 NormalX=0 NormalY=0 NormalZ=1 AngleXU=0 Radius=1 StartAngle=2.35619 EndAngle=5.49779
    g29: ArcOfCircle CenterX=28.7254 CenterY=45 CenterZ=0 NormalX=0 NormalY=0 NormalZ=1 AngleXU=0 Radius=1 StartAngle=5.49779 EndAngle=8.63938
    g30: LineSegment StartX=26.5683 StartY=44.2571 StartZ=0 EndX=28.0183 EndY=45.7071 EndZ=0
    g31: LineSegment StartX=27.9825 StartY=42.8429 StartZ=0 EndX=29.4325 EndY=44.2929 EndZ=0
    g32: ArcOfCircle CenterX=30.6435 CenterY=41.9683 CenterZ=0 NormalX=0 NormalY=0 NormalZ=1 AngleXU=0 Radius=1 StartAngle=2.35619 EndAngle=5.49779
    g33: ArcOfCircle CenterX=35.8725 CenterY=47.1973 CenterZ=0 NormalX=0 NormalY=0 NormalZ=1 AngleXU=0 Radius=1 StartAngle=5.49779 EndAngle=8.63938
    g34: LineSegment StartX=29.9364 StartY=42.6755 StartZ=0 EndX=35.1654 EndY=47.9044 EndZ=0
    g35: LineSegment StartX=31.3506 StartY=41.2612 StartZ=0 EndX=36.5796 EndY=46.4902 EndZ=0
    g36: ArcOfCircle CenterX=31.8017 CenterY=48.0762 CenterZ=0 NormalX=0 NormalY=0 NormalZ=1 AngleXU=0 Radius=1 StartAngle=2.35619 EndAngle=5.49779
    g37: ArcOfCircle CenterX=35.7 CenterY=51.9746 CenterZ=0 NormalX=0 NormalY=0 NormalZ=1 AngleXU=0 Radius=1 StartAngle=5.49779 EndAngle=8.63938
    g38: LineSegment StartX=31.0946 StartY=48.7833 StartZ=0 EndX=34.9929 EndY=52.6817 EndZ=0
    g39: LineSegment StartX=32.5088 StartY=47.3691 StartZ=0 EndX=36.4071 EndY=51.2674 EndZ=0
    g40: ArcOfCircle CenterX=39.5014 CenterY=55.7759 CenterZ=0 NormalX=0 NormalY=0 NormalZ=1 AngleXU=0 Radius=1 StartAngle=2.35619 EndAngle=5.49779
    g41: ArcOfCircle CenterX=43.1254 CenterY=59.4 CenterZ=0 NormalX=0 NormalY=0 NormalZ=1 AngleXU=0 Radius=1 StartAngle=5.49779 EndAngle=8.63938
    g42: LineSegment StartX=38.7943 StartY=56.483 StartZ=0 EndX=42.4183 EndY=60.1071 EndZ=0
    g43: LineSegment StartX=40.2085 StartY=55.0688 StartZ=0 EndX=43.8326 EndY=58.6929 EndZ=0
    g44: ArcOfCircle CenterX=31 CenterY=37.3751 CenterZ=0 NormalX=0 NormalY=0 NormalZ=1 AngleXU=0 Radius=1 StartAngle=2.35619 EndAngle=5.49779
    g45: ArcOfCircle CenterX=38.5822 CenterY=44.9572 CenterZ=0 NormalX=0 NormalY=0 NormalZ=1 AngleXU=0 Radius=1 StartAngle=5.49779 EndAngle=8.63938
    g46: LineSegment StartX=30.2929 StartY=38.0822 StartZ=0 EndX=37.8751 EndY=45.6643 EndZ=0
    g47: LineSegment StartX=31.7071 StartY=36.668 StartZ=0 EndX=39.2893 EndY=44.2501 EndZ=0
    g48: ArcOfCircle CenterX=36.8447 CenterY=38.27 CenterZ=0 NormalX=0 NormalY=0 NormalZ=1 AngleXU=0 Radius=1 StartAngle=2.35619 EndAngle=5.49779
    g49: ArcOfCircle CenterX=41.3451 CenterY=42.7704 CenterZ=0 NormalX=0 NormalY=0 NormalZ=1 AngleXU=0 Radius=1 StartAngle=5.49779 EndAngle=8.63938
    g50: LineSegment StartX=36.1376 StartY=38.9772 StartZ=0 EndX=40.638 EndY=43.4775 EndZ=0
    g51: LineSegment StartX=37.5518 StartY=37.5629 StartZ=0 EndX=42.0522 EndY=42.0633 EndZ=0
    g52: ArcOfCircle CenterX=40.9834 CenterY=37.459 CenterZ=0 NormalX=0 NormalY=0 NormalZ=1 AngleXU=0 Radius=1 StartAngle=2.35619 EndAngle=5.49779
    g53: ArcOfCircle CenterX=46.0244 CenterY=42.5 CenterZ=0 NormalX=0 NormalY=0 NormalZ=1 AngleXU=0 Radius=1 StartAngle=5.49779 EndAngle=8.63938
    g54: LineSegment StartX=40.2763 StartY=38.1661 StartZ=0 EndX=45.3173 EndY=43.2071 EndZ=0
    g55: LineSegment StartX=41.6905 StartY=36.7519 StartZ=0 EndX=46.7315 EndY=41.7929 EndZ=0
    g56: ArcOfCircle CenterX=47.2242 CenterY=38.75 CenterZ=0 NormalX=0 NormalY=0 NormalZ=1 AngleXU=0 Radius=1 StartAngle=2.35619 EndAngle=5.49779
    g57: ArcOfCircle CenterX=50.9742 CenterY=42.5 CenterZ=0 NormalX=0 NormalY=0 NormalZ=1 AngleXU=0 Radius=1 StartAngle=5.49779 EndAngle=8.63938
    g58: LineSegment StartX=46.5171 StartY=39.4571 StartZ=0 EndX=50.2671 EndY=43.2071 EndZ=0
    g59: LineSegment StartX=47.9313 StartY=38.0429 StartZ=0 EndX=51.6813 EndY=41.7929 EndZ=0
    g60: ArcOfCircle CenterX=50 CenterY=36.5761 CenterZ=0 NormalX=0 NormalY=0 NormalZ=1 AngleXU=0 Radius=1 StartAngle=2.35619 EndAngle=5.49779
    g61: ArcOfCircle CenterX=54.2571 CenterY=40.8332 CenterZ=0 NormalX=0 NormalY=0 NormalZ=1 AngleXU=0 Radius=1 StartAngle=5.49779 EndAngle=8.63938
    g62: LineSegment StartX=49.2929 StartY=37.2832 StartZ=0 EndX=53.55 EndY=41.5403 EndZ=0
    g63: LineSegment StartX=50.7071 StartY=35.869 StartZ=0 EndX=54.9642 EndY=40.126 EndZ=0
    g64: ArcOfCircle CenterX=53.5737 CenterY=35.2 CenterZ=0 NormalX=0 NormalY=0 NormalZ=1 AngleXU=0 Radius=1 StartAngle=2.35619 EndAngle=5.49779
    g65: ArcOfCircle CenterX=60.9756 CenterY=42.6019 CenterZ=0 NormalX=0 NormalY=0 NormalZ=1 AngleXU=0 Radius=1 StartAngle=5.49779 EndAngle=8.63938
    g66: LineSegment StartX=52.8666 StartY=35.9071 StartZ=0 EndX=60.2685 EndY=43.309 EndZ=0
    g67: LineSegment StartX=54.2808 StartY=34.4929 StartZ=0 EndX=61.6827 EndY=41.8948 EndZ=0
    g68: ArcOfCircle CenterX=59.0865 CenterY=35.763 CenterZ=0 NormalX=0 NormalY=0 NormalZ=1 AngleXU=0 Radius=1 StartAngle=2.35619 EndAngle=5.49779
    g69: ArcOfCircle CenterX=65.8234 CenterY=42.5 CenterZ=0 NormalX=0 NormalY=0 NormalZ=1 AngleXU=0 Radius=1 StartAngle=5.49779 EndAngle=8.63938
    g70: LineSegment StartX=58.3794 StartY=36.4702 StartZ=0 EndX=65.1163 EndY=43.2071 EndZ=0
    g71: LineSegment StartX=59.7936 StartY=35.0559 StartZ=0 EndX=66.5305 EndY=41.7929 EndZ=0
    g72: ArcOfCircle CenterX=64.8232 CenterY=36.55 CenterZ=0 NormalX=0 NormalY=0 NormalZ=1 AngleXU=0 Radius=1 StartAngle=2.35619 EndAngle=5.49779
    g73: ArcOfCircle CenterX=70.7732 CenterY=42.5 CenterZ=0 NormalX=0 NormalY=0 NormalZ=1 AngleXU=0 Radius=1 StartAngle=5.49779 EndAngle=8.63938
    g74: LineSegment StartX=64.1161 StartY=37.2571 StartZ=0 EndX=70.0661 EndY=43.2071 EndZ=0
    g75: LineSegment StartX=65.5303 StartY=35.8429 StartZ=0 EndX=71.4803 EndY=41.7929 EndZ=0
    g76: ArcOfCircle CenterX=70.6042 CenterY=37.3813 CenterZ=0 NormalX=0 NormalY=0 NormalZ=1 AngleXU=0 Radius=1 StartAngle=2.35619 EndAngle=5.49779
    g77: ArcOfCircle CenterX=79.3593 CenterY=46.1364 CenterZ=0 NormalX=0 NormalY=0 NormalZ=1 AngleXU=0 Radius=1 StartAngle=5.49779 EndAngle=8.63938
    g78: LineSegment StartX=69.8971 StartY=38.0884 StartZ=0 EndX=78.6522 EndY=46.8435 EndZ=0
    g79: LineSegment StartX=71.3113 StartY=36.6742 StartZ=0 EndX=80.0665 EndY=45.4293 EndZ=0
    g80: ArcOfCircle CenterX=76.5441 CenterY=38.3715 CenterZ=0 NormalX=0 NormalY=0 NormalZ=1 AngleXU=0 Radius=1 StartAngle=2.35619 EndAngle=5.49779
    g81: ArcOfCircle CenterX=82.8755 CenterY=44.7028 CenterZ=0 NormalX=0 NormalY=0 NormalZ=1 AngleXU=0 Radius=1 StartAngle=5.49779 EndAngle=8.63938
    g82: LineSegment StartX=75.837 StartY=39.0786 StartZ=0 EndX=82.1684 EndY=45.4099 EndZ=0
    g83: LineSegment StartX=77.2512 StartY=37.6643 StartZ=0 EndX=83.5826 EndY=43.9957 EndZ=0
    g84: ArcOfCircle CenterX=81.8724 CenterY=38.75 CenterZ=0 NormalX=0 NormalY=0 NormalZ=1 AngleXU=0 Radius=1 StartAngle=2.35619 EndAngle=5.49779
    g85: ArcOfCircle CenterX=88.3928 CenterY=45.2704 CenterZ=0 NormalX=0 NormalY=0 NormalZ=1 AngleXU=0 Radius=1 StartAngle=5.49779 EndAngle=8.63938
    g86: LineSegment StartX=81.1653 StartY=39.4571 StartZ=0 EndX=87.6857 EndY=45.9775 EndZ=0
    g87: LineSegment StartX=82.5795 StartY=38.0429 StartZ=0 EndX=89.0999 EndY=44.5633 EndZ=0
    g88: ArcOfCircle CenterX=86.449 CenterY=38.3769 CenterZ=0 NormalX=0 NormalY=0 NormalZ=1 AngleXU=0 Radius=1 StartAngle=2.35619 EndAngle=5.49779
    g89: ArcOfCircle CenterX=95.1543 CenterY=47.0821 CenterZ=0 NormalX=0 NormalY=0 NormalZ=1 AngleXU=0 Radius=1 StartAngle=5.49779 EndAngle=8.63938
    g90: LineSegment StartX=85.7419 StartY=39.084 StartZ=0 EndX=94.4472 EndY=47.7892 EndZ=0
    g91: LineSegment StartX=87.1561 StartY=37.6697 StartZ=0 EndX=95.8614 EndY=46.375 EndZ=0
    g92: ArcOfCircle CenterX=93.3548 CenterY=40.3329 CenterZ=0 NormalX=0 NormalY=0 NormalZ=1 AngleXU=0 Radius=1 StartAngle=2.35619 EndAngle=5.49779
    g93: ArcOfCircle CenterX=98.9105 CenterY=45.8885 CenterZ=0 NormalX=0 NormalY=0 NormalZ=1 AngleXU=0 Radius=1 StartAngle=5.49779 EndAngle=8.63938
    g94: LineSegment StartX=92.6477 StartY=41.04 StartZ=0 EndX=98.2034 EndY=46.5957 EndZ=0
    g95: LineSegment StartX=94.0619 StartY=39.6258 StartZ=0 EndX=99.6176 EndY=45.1814 EndZ=0
    g96: ArcOfCircle CenterX=97.7715 CenterY=39.7999 CenterZ=0 NormalX=0 NormalY=0 NormalZ=1 AngleXU=0 Radius=1 StartAngle=2.35619 EndAngle=5.49779
    g97: ArcOfCircle CenterX=102.645 CenterY=44.6729 CenterZ=0 NormalX=0 NormalY=0 NormalZ=1 AngleXU=0 Radius=1 StartAngle=5.49779 EndAngle=8.63938
    g98: LineSegment StartX=97.0644 StartY=40.507 StartZ=0 EndX=101.937 EndY=45.38 EndZ=0
    g99: LineSegment StartX=98.4786 StartY=39.0927 StartZ=0 EndX=103.352 EndY=43.9658 EndZ=0
    g100: ArcOfCircle CenterX=103.871 CenterY=40.95 CenterZ=0 NormalX=0 NormalY=0 NormalZ=1 AngleXU=0 Radius=1 StartAngle=2.35619 EndAngle=5.49779
    g101: ArcOfCircle CenterX=110.363 CenterY=47.4412 CenterZ=0 NormalX=0 NormalY=0 NormalZ=1 AngleXU=0 Radius=1 StartAngle=5.49779 EndAngle=8.63938
    g102: LineSegment StartX=103.164 StartY=41.6571 StartZ=0 EndX=109.656 EndY=48.1483 EndZ=0
    g103: LineSegment StartX=104.579 StartY=40.2429 StartZ=0 EndX=111.07 EndY=46.7341 EndZ=0
    g104: ArcOfCircle CenterX=99.0064 CenterY=50.9342 CenterZ=0 NormalX=0 NormalY=0 NormalZ=1 AngleXU=0 Radius=1 StartAngle=2.35619 EndAngle=5.49779
    g105: ArcOfCircle CenterX=101.374 CenterY=53.3017 CenterZ=0 NormalX=0 NormalY=0 NormalZ=1 AngleXU=0 Radius=1 StartAngle=5.49779 EndAngle=8.63938
    g106: LineSegment StartX=98.2993 StartY=51.6413 StartZ=0 EndX=100.667 EndY=54.0088 EndZ=0
    g107: LineSegment StartX=99.7135 StartY=50.2271 StartZ=0 EndX=102.081 EndY=52.5946 EndZ=0
    g108: ArcOfCircle CenterX=46.2157 CenterY=57.5405 CenterZ=0 NormalX=0 NormalY=0 NormalZ=1 AngleXU=0 Radius=1 StartAngle=2.35619 EndAngle=5.49779
    g109: ArcOfCircle CenterX=48.0752 CenterY=59.4 CenterZ=0 NormalX=0 NormalY=0 NormalZ=1 AngleXU=0 Radius=1 StartAngle=5.49779 EndAngle=8.63938
    g110: LineSegment StartX=45.5086 StartY=58.2476 StartZ=0 EndX=47.3681 EndY=60.1071 EndZ=0
    g111: LineSegment StartX=46.9228 StartY=56.8334 StartZ=0 EndX=48.7823 EndY=58.6929 EndZ=0
    g112: ArcOfCircle CenterX=50.157 CenterY=56.532 CenterZ=0 NormalX=0 NormalY=0 NormalZ=1 AngleXU=0 Radius=1 StartAngle=2.35619 EndAngle=5.49779
    g113: ArcOfCircle CenterX=53.0249 CenterY=59.4 CenterZ=0 NormalX=0 NormalY=0 NormalZ=1 AngleXU=0 Radius=1 StartAngle=5.49779 EndAngle=8.63938
    g114: LineSegment StartX=49.4499 StartY=57.2391 StartZ=0 EndX=52.3178 EndY=60.1071 EndZ=0
    g115: LineSegment StartX=50.8641 StartY=55.8249 StartZ=0 EndX=53.732 EndY=58.6929 EndZ=0
    g116: ArcOfCircle CenterX=56.5247 CenterY=57.95 CenterZ=0 NormalX=0 NormalY=0 NormalZ=1 AngleXU=0 Radius=1 StartAngle=2.35619 EndAngle=5.49779
    g117: ArcOfCircle CenterX=57.9747 CenterY=59.4 CenterZ=0 NormalX=0 NormalY=0 NormalZ=1 AngleXU=0 Radius=1 StartAngle=5.49779 EndAngle=8.63938
    g118: LineSegment StartX=55.8176 StartY=58.6571 StartZ=0 EndX=57.2676 EndY=60.1071 EndZ=0
    g119: LineSegment StartX=57.2318 StartY=57.2429 StartZ=0 EndX=58.6818 EndY=58.6929 EndZ=0
    g120: ArcOfCircle CenterX=60.0048 CenterY=56.4804 CenterZ=0 NormalX=0 NormalY=0 NormalZ=1 AngleXU=0 Radius=1 StartAngle=2.35619 EndAngle=5.49779
    g121: ArcOfCircle CenterX=62.9244 CenterY=59.4 CenterZ=0 NormalX=0 NormalY=0 NormalZ=1 AngleXU=0 Radius=1 StartAngle=5.49779 EndAngle=8.63938
    g122: LineSegment StartX=59.2977 StartY=57.1875 StartZ=0 EndX=62.2173 EndY=60.1071 EndZ=0
    g123: LineSegment StartX=60.7119 StartY=55.7733 StartZ=0 EndX=63.6315 EndY=58.6929 EndZ=0
    g124: ArcOfCircle CenterX=66.0737 CenterY=57.5995 CenterZ=0 NormalX=0 NormalY=0 NormalZ=1 AngleXU=0 Radius=1 StartAngle=2.35619 EndAngle=5.49779
    g125: ArcOfCircle CenterX=67.914 CenterY=59.4398 CenterZ=0 NormalX=0 NormalY=0 NormalZ=1 AngleXU=0 Radius=1 StartAngle=5.49779 EndAngle=8.63938
    g126: LineSegment StartX=65.3666 StartY=58.3066 StartZ=0 EndX=67.2069 EndY=60.1469 EndZ=0
    g127: LineSegment StartX=66.7808 StartY=56.8924 StartZ=0 EndX=68.6211 EndY=58.7327 EndZ=0
    g128: ArcOfCircle CenterX=69.5879 CenterY=56.1639 CenterZ=0 NormalX=0 NormalY=0 NormalZ=1 AngleXU=0 Radius=1 StartAngle=2.35619 EndAngle=5.49779
    g129: ArcOfCircle CenterX=73.216 CenterY=59.7921 CenterZ=0 NormalX=0 NormalY=0 NormalZ=1 AngleXU=0 Radius=1 StartAngle=5.49779 EndAngle=8.63938
    g130: LineSegment StartX=68.8808 StartY=56.871 StartZ=0 EndX=72.5089 EndY=60.4992 EndZ=0
    g131: LineSegment StartX=70.295 StartY=55.4568 StartZ=0 EndX=73.9231 EndY=59.085 EndZ=0
    g132: ArcOfCircle CenterX=76.1106 CenterY=57.7369 CenterZ=0 NormalX=0 NormalY=0 NormalZ=1 AngleXU=0 Radius=1 StartAngle=2.35619 EndAngle=5.49779
    g133: ArcOfCircle CenterX=78.9646 CenterY=60.5909 CenterZ=0 NormalX=0 NormalY=0 NormalZ=1 AngleXU=0 Radius=1 StartAngle=5.49779 EndAngle=8.63938
    g134: LineSegment StartX=75.4035 StartY=58.444 StartZ=0 EndX=78.2575 EndY=61.298 EndZ=0
    g135: LineSegment StartX=76.8177 StartY=57.0298 StartZ=0 EndX=79.6717 EndY=59.8838 EndZ=0
    g136: ArcOfCircle CenterX=81.2873 CenterY=57.9639 CenterZ=0 NormalX=0 NormalY=0 NormalZ=1 AngleXU=0 Radius=1 StartAngle=2.35619 EndAngle=5.49779
    g137: ArcOfCircle CenterX=85.3188 CenterY=61.9954 CenterZ=0 NormalX=0 NormalY=0 NormalZ=1 AngleXU=0 Radius=1 StartAngle=5.49779 EndAngle=8.63938
    g138: LineSegment StartX=80.5802 StartY=58.671 StartZ=0 EndX=84.6117 EndY=62.7025 EndZ=0
    g139: LineSegment StartX=81.9944 StartY=57.2567 StartZ=0 EndX=86.0259 EndY=61.2883 EndZ=0
    g140: ArcOfCircle CenterX=88.5064 CenterY=60.2332 CenterZ=0 NormalX=0 NormalY=0 NormalZ=1 AngleXU=0 Radius=1 StartAngle=2.35619 EndAngle=5.49779
    g141: ArcOfCircle CenterX=92.5869 CenterY=64.3137 CenterZ=0 NormalX=0 NormalY=0 NormalZ=1 AngleXU=0 Radius=1 StartAngle=5.49779 EndAngle=8.63938
    g142: LineSegment StartX=87.7993 StartY=60.9403 StartZ=0 EndX=91.8798 EndY=65.0208 EndZ=0
    g143: LineSegment StartX=89.2135 StartY=59.5261 StartZ=0 EndX=93.294 EndY=63.6066 EndZ=0
    g144: ArcOfCircle CenterX=96.0904 CenterY=62.8675 CenterZ=0 NormalX=0 NormalY=0 NormalZ=1 AngleXU=0 Radius=1 StartAngle=2.35619 EndAngle=5.49779
    g145: ArcOfCircle CenterX=101.56 CenterY=68.3367 CenterZ=0 NormalX=0 NormalY=0 NormalZ=1 AngleXU=0 Radius=1 StartAngle=5.49779 EndAngle=8.63938
    g146: LineSegment StartX=95.3833 StartY=63.5746 StartZ=0 EndX=100.853 EndY=69.0438 EndZ=0
    g147: LineSegment StartX=96.7975 StartY=62.1603 StartZ=0 EndX=102.267 EndY=67.6296 EndZ=0
    g148: ArcOfCircle CenterX=106.471 CenterY=68.2983 CenterZ=0 NormalX=0 NormalY=0 NormalZ=1 AngleXU=0 Radius=1 StartAngle=2.35619 EndAngle=5.49779
    g149: ArcOfCircle CenterX=110.09 CenterY=71.9177 CenterZ=0 NormalX=0 NormalY=0 NormalZ=1 AngleXU=0 Radius=1 StartAngle=5.49779 EndAngle=8.63938
    g150: LineSegment StartX=105.764 StartY=69.0054 StartZ=0 EndX=109.383 EndY=72.6248 EndZ=0
    g151: LineSegment StartX=107.178 StartY=67.5912 StartZ=0 EndX=110.797 EndY=71.2106 EndZ=0
    g152: ArcOfCircle CenterX=109.744 CenterY=66.6211 CenterZ=0 NormalX=0 NormalY=0 NormalZ=1 AngleXU=0 Radius=1 StartAngle=2.35619 EndAngle=5.49779
    g153: ArcOfCircle CenterX=111.902 CenterY=68.7797 CenterZ=0 NormalX=0 NormalY=0 NormalZ=1 AngleXU=0 Radius=1 StartAngle=5.49779 EndAngle=8.63938
    g154: LineSegment StartX=109.036 StartY=67.3282 StartZ=0 EndX=111.195 EndY=69.4868 EndZ=0
    g155: LineSegment StartX=110.451 StartY=65.914 StartZ=0 EndX=112.609 EndY=68.0726 EndZ=0
    g156: ArcOfCircle CenterX=111.856 CenterY=63.7836 CenterZ=0 NormalX=0 NormalY=0 NormalZ=1 AngleXU=0 Radius=1 StartAngle=2.35619 EndAngle=5.49779
    g157: ArcOfCircle CenterX=113.714 CenterY=65.6416 CenterZ=0 NormalX=0 NormalY=0 NormalZ=1 AngleXU=0 Radius=1 StartAngle=5.49779 EndAngle=8.63938
    g158: LineSegment StartX=111.149 StartY=64.4907 StartZ=0 EndX=113.007 EndY=66.3488 EndZ=0
    g159: LineSegment StartX=112.563 StartY=63.0765 StartZ=0 EndX=114.421 EndY=64.9345 EndZ=0
    g160: ArcOfCircle CenterX=114.206 CenterY=61.1845 CenterZ=0 NormalX=0 NormalY=0 NormalZ=1 AngleXU=0 Radius=1 StartAngle=2.35619 EndAngle=5.49779
    g161: ArcOfCircle CenterX=115.526 CenterY=62.5036 CenterZ=0 NormalX=0 NormalY=0 NormalZ=1 AngleXU=0 Radius=1 StartAngle=5.49779 EndAngle=8.63938
    g162: LineSegment StartX=113.499 StartY=61.8916 StartZ=0 EndX=114.818 EndY=63.2107 EndZ=0
    g163: LineSegment StartX=114.914 StartY=60.4774 StartZ=0 EndX=116.233 EndY=61.7965 EndZ=0
    g164: ArcOfCircle CenterX=115.61 CenterY=57.6386 CenterZ=0 NormalX=0 NormalY=0 NormalZ=1 AngleXU=0 Radius=1 StartAngle=2.35619 EndAngle=5.49779
    g165: ArcOfCircle CenterX=117.337 CenterY=59.3656 CenterZ=0 NormalX=0 NormalY=0 NormalZ=1 AngleXU=0 Radius=1 StartAngle=5.49779 EndAngle=8.63938
    g166: LineSegment StartX=114.903 StartY=58.3457 StartZ=0 EndX=116.63 EndY=60.0727 EndZ=0
    g167: LineSegment StartX=116.317 StartY=56.9315 StartZ=0 EndX=118.044 EndY=58.6585 EndZ=0
    g168: ArcOfCircle CenterX=118.119 CenterY=55.1978 CenterZ=0 NormalX=0 NormalY=0 NormalZ=1 AngleXU=0 Radius=1 StartAngle=2.35619 EndAngle=5.49779
    g169: ArcOfCircle CenterX=119.149 CenterY=56.2276 CenterZ=0 NormalX=0 NormalY=0 NormalZ=1 AngleXU=0 Radius=1 StartAngle=5.49779 EndAngle=8.63938
    g170: LineSegment StartX=117.412 StartY=55.9049 StartZ=0 EndX=118.442 EndY=56.9347 EndZ=0
    g171: LineSegment StartX=118.826 StartY=54.4907 StartZ=0 EndX=119.856 EndY=55.5205 EndZ=0
  constraints (428):
    c: Tangent(g0,g2) = 1.5708
    c: Tangent(g0,g3) = -1.5708
    c: Tangent(g1,g2) = 1.5708
    c: Tangent(g1,g3) = -1.5708
    c: Equal(g0,g1)
    c: Angle(g-1,g2) = 0.785398
    c: Radius(g0) = 1
    c: Distance(g0,g-3) = 1.5
    c: Tangent(g4,g6) = 1.5708
    c: Tangent(g4,g7) = -1.5708
    c: Tangent(g5,g6) = 1.5708
    c: Tangent(g5,g7) = -1.5708
    c: Equal(g4,g5)
    c: Angle(g-1,g6) = 0.785398
    c: Radius(g4) = 1
    c: Distance(g3,g6) = 1.5
    c: Distance(g-5,g4) = 1.5
    c: Distance(g4,g-4) = 1.5
    c: Distance(g1,g-6) = 1.5
    c: Distance(g5,g-6) = 1.5
    c: Tangent(g8,g10) = 1.5708
    c: Tangent(g8,g11) = -1.5708
    c: Tangent(g9,g10) = 1.5708
    c: Tangent(g9,g11) = -1.5708
    c: Equal(g8,g9)
    c: Angle(g-1,g10) = 0.785398
    c: Radius(g8) = 1
    c: Tangent(g12,g14) = 1.5708
    c: Tangent(g12,g15) = -1.5708
    c: Tangent(g13,g14) = 1.5708
    c: Tangent(g13,g15) = -1.5708
    c: Equal(g12,g13)
    c: Angle(g-1,g14) = 0.785398
    c: Radius(g12) = 1
    c: Tangent(g16,g18) = 1.5708
    c: Tangent(g16,g19) = -1.5708
    c: Tangent(g17,g18) = 1.5708
    c: Tangent(g17,g19) = -1.5708
    c: Equal(g16,g17)
    c: Angle(g-1,g18) = 0.785398
    c: Radius(g16) = 1
    c: Tangent(g20,g22) = 1.5708
    c: Tangent(g20,g23) = -1.5708
    c: Tangent(g21,g22) = 1.5708
    c: Tangent(g21,g23) = -1.5708
    c: Equal(g20,g21)
    c: Angle(g-1,g22) = 0.785398
    c: Radius(g20) = 1
    c: Tangent(g24,g26) = 1.5708
    c: Tangent(g24,g27) = -1.5708
    c: Tangent(g25,g26) = 1.5708
    c: Tangent(g25,g27) = -1.5708
    c: Equal(g24,g25)
    c: Angle(g-1,g26) = 0.785398
    c: Radius(g24) = 1
    c: Distance(g10,g7) = 1.5
    c: Distance(g14,g11) = 1.5
    c: Distance(g18,g15) = 1
    c: Distance(g22,g19) = 1.5
    c: Distance(g26,g23) = 1.5
    c: Distance(g8,g-5) = 1.5
    c: Distance(g9,g-6) = 1.5
    c: Distance(g13,g-6) = 1.5
    c: Distance(g17,g-6) = 1.5
    c: Distance(g12,g-10) = 1.5
    c: Distance(g16,g-7) = 1.5
    c: Distance(g20,g-8) = 1.5
    c: Distance(g21,g-6) = 1.5
    c: Distance(g25,g-6) = 1.5
    c: Distance(g24,g-8) = 1.5
    c: Tangent(g28,g30) = 1.5708
    c: Tangent(g28,g31) = -1.5708
    c: Tangent(g29,g30) = 1.5708
    c: Tangent(g29,g31) = -1.5708
    c: Equal(g28,g29)
    c: Angle(g-1,g30) = 0.785398
    c: Radius(g28) = 1
    c: Distance(g27,g30) = 1.5
    c: Distance(g28,g-9) = 1.5
    c: Distance(g29,g-6) = 1.5
    c: Tangent(g32,g34) = 1.5708
    c: Tangent(g32,g35) = -1.5708
    c: Tangent(g33,g34) = 1.5708
    c: Tangent(g33,g35) = -1.5708
    c: Equal(g32,g33)
    c: Angle(g-1,g34) = 0.785398
    c: Radius(g32) = 1
    c: Distance(g34,g31) = 1.5
    c: Distance(g32,g-13) = 1.5
    c: Distance(g-14,g33) = 1.5
    c: Tangent(g36,g38) = 1.5708
    c: Tangent(g36,g39) = -1.5708
    c: Tangent(g37,g38) = 1.5708
    c: Tangent(g37,g39) = -1.5708
    c: Equal(g36,g37)
    c: Angle(g-1,g38) = 0.785398
    c: Radius(g36) = 1
    c: Distance(g34,g39) = 1.5
    c: Distance(g36,g-15) = 1.5
    c: Distance(g37,g-11) = 1.5
    c: Tangent(g40,g42) = 1.5708
    c: Tangent(g40,g43) = -1.5708
    c: Tangent(g41,g42) = 1.5708
    c: Tangent(g41,g43) = -1.5708
    c: Equal(g40,g41)
    c: Radius(g40) = 1
    c: Tangent(g43,g39)
    c: Distance(g41,g-18) = 1.5
    c: Distance(g40,g-17) = 1.5
    c: Tangent(g44,g46) = 1.5708
    c: Tangent(g44,g47) = -1.5708
    c: Tangent(g45,g46) = 1.5708
    c: Tangent(g45,g47) = -1.5708
    c: Equal(g44,g45)
    c: Angle(g-1,g46) = 0.785398
    c: Radius(g44) = 1
    c: Tangent(g48,g50) = 1.5708
    c: Tangent(g48,g51) = -1.5708
    c: Tangent(g49,g50) = 1.5708
    c: Tangent(g49,g51) = -1.5708
    c: Equal(g48,g49)
    c: Angle(g-1,g50) = 0.785398
    c: Radius(g48) = 1
    c: Tangent(g52,g54) = 1.5708
    c: Tangent(g52,g55) = -1.5708
    c: Tangent(g53,g54) = 1.5708
    c: Tangent(g53,g55) = -1.5708
    c: Equal(g52,g53)
    c: Angle(g-1,g54) = 0.785398
    c: Radius(g52) = 1
    c: Distance(g35,g46) = 1.5
    c: Distance(g50,g47) = 1.5
    c: Distance(g54,g51) = 1.5
    c: Distance(g44,g-24) = 1.5
    c: Distance(g45,g-19) = 1.5
    c: Distance(g48,g-21) = 1.5
    c: Distance(g49,g-19) = 1.5
    c: Distance(g52,g-21) = 1.5
    c: Distance(g53,g-20) = 1.5
    c: Tangent(g56,g58) = 1.5708
    c: Tangent(g56,g59) = -1.5708
    c: Tangent(g57,g58) = 1.5708
    c: Tangent(g57,g59) = -1.5708
    c: Equal(g56,g57)
    c: Angle(g-1,g58) = 0.785398
    c: Radius(g56) = 1
    c: Tangent(g60,g62) = 1.5708
    c: Tangent(g60,g63) = -1.5708
    c: Tangent(g61,g62) = 1.5708
    c: Tangent(g61,g63) = -1.5708
    c: Equal(g60,g61)
    c: Angle(g-1,g62) = 0.785398
    c: Radius(g60) = 1
    c: Distance(g55,g58) = 1.5
    c: Distance(g62,g59) = 1.5
    c: Tangent(g64,g66) = 1.5708
    c: Tangent(g64,g67) = -1.5708
    c: Tangent(g65,g66) = 1.5708
    c: Tangent(g65,g67) = -1.5708
    c: Equal(g64,g65)
    c: Angle(g-1,g66) = 0.785398
    c: Radius(g64) = 1
    c: Tangent(g68,g70) = 1.5708
    c: Tangent(g68,g71) = -1.5708
    c: Tangent(g69,g70) = 1.5708
    c: Tangent(g69,g71) = -1.5708
    c: Equal(g68,g69)
    c: Angle(g-1,g70) = 0.785398
    c: Radius(g68) = 1
    c: Distance(g57,g-20) = 1.5
    c: Distance(g56,g-22) = 1.5
    c: Distance(g60,g-25) = 1.5
    c: Distance(g61,g-27) = 0.1
    c: Distance(g63,g66) = 1.5
    c: Distance(g70,g67) = 1.5
    c: Distance(g64,g-29) = 1.5
    c: Distance(g65,g-30) = 1.5
    c: Distance(g68,g-26) = 1.5
    c: Distance(g69,g-28) = 1.5
    c: Tangent(g72,g74) = 1.5708
    c: Tangent(g72,g75) = -1.5708
    c: Tangent(g73,g74) = 1.5708
    c: Tangent(g73,g75) = -1.5708
    c: Equal(g72,g73)
    c: Angle(g-1,g74) = 0.785398
    c: Radius(g72) = 1
    c: Tangent(g76,g78) = 1.5708
    c: Tangent(g76,g79) = -1.5708
    c: Tangent(g77,g78) = 1.5708
    c: Tangent(g77,g79) = -1.5708
    c: Equal(g76,g77)
    c: Angle(g-1,g78) = 0.785398
    c: Radius(g76) = 1
    c: Tangent(g80,g82) = 1.5708
    c: Tangent(g80,g83) = -1.5708
    c: Tangent(g81,g82) = 1.5708
    c: Tangent(g81,g83) = -1.5708
    c: Equal(g80,g81)
    c: Angle(g-1,g82) = 0.785398
    c: Radius(g80) = 1
    c: Tangent(g84,g86) = 1.5708
    c: Tangent(g84,g87) = -1.5708
    c: Tangent(g85,g86) = 1.5708
    c: Tangent(g85,g87) = -1.5708
    c: Equal(g84,g85)
    c: Angle(g-1,g86) = 0.785398
    c: Radius(g84) = 1
    c: Distance(g71,g74) = 1.5
    c: Distance(g78,g75) = 1.5
    c: Distance(g73,g-28) = 1.5
    c: Distance(g82,g79) = 1.5
    c: Distance(g86,g83) = 1.5
    c: Distance(g72,g-31) = 1.5
    c: Distance(g76,g-32) = 1.5
    c: Distance(g77,g-35) = 1.5
    c: Distance(g80,g-33) = 1.5
    c: Distance(g81,g-37) = 1.5
    c: Distance(g85,g-38) = 1.5
    c: Distance(g84,g-34) = 1.5
    c: Tangent(g88,g90) = 1.5708
    c: Tangent(g88,g91) = -1.5708
    c: Tangent(g89,g90) = 1.5708
    c: Tangent(g89,g91) = -1.5708
    c: Equal(g88,g89)
    c: Angle(g-1,g90) = 0.785398
    c: Radius(g88) = 1
    c: Tangent(g92,g94) = 1.5708
    c: Tangent(g92,g95) = -1.5708
    c: Tangent(g93,g94) = 1.5708
    c: Tangent(g93,g95) = -1.5708
    c: Equal(g92,g93)
    c: Angle(g-1,g94) = 0.785398
    c: Radius(g92) = 1
    c: Distance(g87,g90) = 1.5
    c: Distance(g94,g91) = 1.5
    c: Distance(g88,g-41) = 1.5
    c: Distance(g92,g-40) = 1.5
    c: Distance(g89,g-38) = 1.5
    c: Distance(g93,g-42) = 0.1
    c: Tangent(g96,g98) = 1.5708
    c: Tangent(g96,g99) = -1.5708
    c: Tangent(g97,g98) = 1.5708
    c: Tangent(g97,g99) = -1.5708
    c: Equal(g96,g97)
    c: Angle(g-1,g98) = 0.785398
    c: Radius(g96) = 1
    c: Tangent(g100,g102) = 1.5708
    c: Tangent(g100,g103) = -1.5708
    c: Tangent(g101,g102) = 1.5708
    c: Tangent(g101,g103) = -1.5708
    c: Equal(g100,g101)
    c: Angle(g-1,g102) = 0.785398
    c: Radius(g100) = 1
    c: Distance(g95,g98) = 1.5
    c: Distance(g102,g99) = 1.5
    c: Distance(g96,g-40) = 1.5
    c: Distance(g97,g-42) = 0.1
    c: Distance(g101,g-44) = 1.5
    c: Distance(g100,g-43) = 1.5
    c: Tangent(g104,g106) = 1.5708
    c: Tangent(g104,g107) = -1.5708
    c: Tangent(g105,g106) = 1.5708
    c: Tangent(g105,g107) = -1.5708
    c: Equal(g104,g105)
    c: Radius(g104) = 1
    c: Tangent(g107,g91)
    c: Distance(g104,g-47) = 1.5
    c: Distance(g105,g-46) = 1.5
    c: Tangent(g108,g110) = 1.5708
    c: Tangent(g108,g111) = -1.5708
    c: Tangent(g109,g110) = 1.5708
    c: Tangent(g109,g111) = -1.5708
    c: Equal(g108,g109)
    c: Angle(g-1,g110) = 0.785398
    c: Radius(g108) = 1
    c: Tangent(g112,g114) = 1.5708
    c: Tangent(g112,g115) = -1.5708
    c: Tangent(g113,g114) = 1.5708
    c: Tangent(g113,g115) = -1.5708
    c: Equal(g112,g113)
    c: Angle(g-1,g114) = 0.785398
    c: Radius(g112) = 1
    c: Tangent(g116,g118) = 1.5708
    c: Tangent(g116,g119) = -1.5708
    c: Tangent(g117,g118) = 1.5708
    c: Tangent(g117,g119) = -1.5708
    c: Equal(g116,g117)
    c: Angle(g-1,g118) = 0.785398
    c: Radius(g116) = 1
    c: Tangent(g120,g122) = 1.5708
    c: Tangent(g120,g123) = -1.5708
    c: Tangent(g121,g122) = 1.5708
    c: Tangent(g121,g123) = -1.5708
    c: Equal(g120,g121)
    c: Angle(g-1,g122) = 0.785398
    c: Radius(g120) = 1
    c: Distance(g43,g110) = 1.5
    c: Distance(g114,g111) = 1.5
    c: Distance(g118,g115) = 1.5
    c: Distance(g122,g119) = 1.5
    c: Distance(g109,g-18) = 1.5
    c: Distance(g113,g-18) = 1.5
    c: Distance(g-48,g108) = 1.5
    c: Distance(g112,g-48) = 1.5
    c: Distance(g116,g-49) = 1.5
    c: Distance(g117,g-18) = 1.5
    c: Distance(g-50,g120) = 1.5
    c: Distance(g121,g-18) = 1.5
    c: Tangent(g124,g126) = 1.5708
    c: Tangent(g124,g127) = -1.5708
    c: Tangent(g125,g126) = 1.5708
    c: Tangent(g125,g127) = -1.5708
    c: Equal(g124,g125)
    c: Angle(g-1,g126) = 0.785398
    c: Radius(g124) = 1
    c: Tangent(g128,g130) = 1.5708
    c: Tangent(g128,g131) = -1.5708
    c: Tangent(g129,g130) = 1.5708
    c: Tangent(g129,g131) = -1.5708
    c: Equal(g128,g129)
    c: Angle(g-1,g130) = 0.785398
    c: Radius(g128) = 1
    c: Tangent(g132,g134) = 1.5708
    c: Tangent(g132,g135) = -1.5708
    c: Tangent(g133,g134) = 1.5708
    c: Tangent(g133,g135) = -1.5708
    c: Equal(g132,g133)
    c: Angle(g-1,g134) = 0.785398
    c: Radius(g132) = 1
    c: Tangent(g136,g138) = 1.5708
    c: Tangent(g136,g139) = -1.5708
    c: Tangent(g137,g138) = 1.5708
    c: Tangent(g137,g139) = -1.5708
    c: Equal(g136,g137)
    c: Angle(g-1,g138) = 0.785398
    c: Radius(g136) = 1
    c: Distance(g123,g126) = 1.5
    c: Distance(g130,g127) = 1.5
    c: Distance(g125,g-52) = 1.5
    c: Distance(g-51,g124) = 1.5
    c: Distance(g-51,g128) = 1.5
    c: Distance(g131,g134) = 1.5
    c: Distance(g138,g135) = 1.5
    c: Distance(g133,g-52) = 1.5
    c: Distance(g129,g-52) = 1.5
    c: Distance(g-56,g132) = 1.5
    c: Distance(g-52,g137) = 1.5
    c: Distance(g136,g-57) = 1.5
    c: Tangent(g140,g142) = 1.5708
    c: Tangent(g140,g143) = -1.5708
    c: Tangent(g141,g142) = 1.5708
    c: Tangent(g141,g143) = -1.5708
    c: Equal(g140,g141)
    c: Angle(g-1,g142) = 0.785398
    c: Radius(g140) = 1
    c: Tangent(g144,g146) = 1.5708
    c: Tangent(g144,g147) = -1.5708
    c: Tangent(g145,g146) = 1.5708
    c: Tangent(g145,g147) = -1.5708
    c: Equal(g144,g145)
    c: Angle(g-1,g146) = 0.785398
    c: Radius(g144) = 1
    c: Distance(g139,g142) = 1.5
    c: Distance(g146,g143) = 1.5
    c: Distance(g140,g-55) = 1.5
    c: Distance(g141,g-52) = 1.5
    c: Distance(g145,g-52) = 1.5
    c: Distance(g144,g-58) = 1.5
    c: Tangent(g148,g150) = 1.5708
    c: Tangent(g148,g151) = -1.5708
    c: Tangent(g149,g150) = 1.5708
    c: Tangent(g149,g151) = -1.5708
    c: Equal(g148,g149)
    c: Angle(g-1,g150) = 0.785398
    c: Radius(g148) = 1
    c: Distance(g147,g150) = 1.5
    c: Distance(g149,g-59) = 1.5
    c: Distance(g148,g-60) = 1.5
    c: Tangent(g152,g154) = 1.5708
    c: Tangent(g152,g155) = -1.5708
    c: Tangent(g153,g154) = 1.5708
    c: Tangent(g153,g155) = -1.5708
    c: Equal(g152,g153)
    c: Angle(g-1,g154) = 0.785398
    c: Radius(g152) = 1
    c: Distance(g151,g154) = 1.5
    c: Distance(g152,g-61) = 1.5
    c: Distance(g153,g-59) = 1.5
    c: Tangent(g156,g158) = 1.5708
    c: Tangent(g156,g159) = -1.5708
    c: Tangent(g157,g158) = 1.5708
    c: Tangent(g157,g159) = -1.5708
    c: Equal(g156,g157)
    c: Angle(g-1,g158) = 0.785398
    c: Radius(g156) = 1
    c: Tangent(g160,g162) = 1.5708
    c: Tangent(g160,g163) = -1.5708
    c: Tangent(g161,g162) = 1.5708
    c: Tangent(g161,g163) = -1.5708
    c: Equal(g160,g161)
    c: Angle(g-1,g162) = 0.785398
    c: Radius(g160) = 1
    c: Tangent(g164,g166) = 1.5708
    c: Tangent(g164,g167) = -1.5708
    c: Tangent(g165,g166) = 1.5708
    c: Tangent(g165,g167) = -1.5708
    c: Equal(g164,g165)
    c: Angle(g-1,g166) = 0.785398
    c: Radius(g164) = 1
    c: Tangent(g168,g170) = 1.5708
    c: Tangent(g168,g171) = -1.5708
    c: Tangent(g169,g170) = 1.5708
    c: Tangent(g169,g171) = -1.5708
    c: Equal(g168,g169)
    c: Angle(g-1,g170) = 0.785398
    c: Radius(g168) = 1
    c: Distance(g155,g158) = 1.5
    c: Distance(g159,g162) = 1.5
    c: Distance(g166,g163) = 1.5
    c: Distance(g170,g167) = 1.5
    c: Distance(g156,g-62) = 1.5
    c: Distance(g161,g-59) = 1.5
    c: Distance(g160,g-62) = 1.5
    c: Distance(g157,g-59) = 1.5
    c: Distance(g165,g-59) = 1.5
    c: Distance(g169,g-59) = 1.5
    c: Distance(g164,g-64) = 1.5
    c: Distance(g168,g-65) = 1.5
FEATURE [PartDesign::Pocket] Pocket002
  BaseFeature = -> LinearPattern001
  Direction = (0,0,1)
  Length = 5
  Length2 = 5
  Profile = -> Sketch006
  ReferenceAxis = -> Sketch006 [N_Axis]
  Suppressed = false
  Type = 1
FEATURE [Sketcher::SketchObject] Sketch007
  AttachmentSupport = -> [Pocket002]
  ExternalGeometry = -> [Pocket002]
  FullyConstrained = true
  MapMode = 5
  Placement = pos=(0,0,0) rot=(1,0,0;3.14159rad)
  sketch-geometry (89):
    g0: ArcOfCircle CenterX=107.2 CenterY=-3.8 CenterZ=0 NormalX=0 NormalY=0 NormalZ=1 AngleXU=0 Radius=1.25 StartAngle=3.14159 EndAngle=6.28319
    g1: ArcOfCircle CenterX=107.2 CenterY=24.1 CenterZ=0 NormalX=0 NormalY=0 NormalZ=1 AngleXU=0 Radius=1.25 StartAngle=9e-16 EndAngle=3.14159
    g2: LineSegment StartX=105.95 StartY=-3.8 StartZ=0 EndX=105.95 EndY=24.1 EndZ=0
    g3: LineSegment StartX=108.45 StartY=-3.8 StartZ=0 EndX=108.45 EndY=24.1 EndZ=0
    g4: ArcOfCircle CenterX=122.44 CenterY=-3.8 CenterZ=0 NormalX=0 NormalY=0 NormalZ=1 AngleXU=0 Radius=1.25 StartAngle=3.14159 EndAngle=6.28319
    g5: ArcOfCircle CenterX=122.44 CenterY=24.1 CenterZ=0 NormalX=0 NormalY=0 NormalZ=1 AngleXU=0 Radius=1.25 StartAngle=0 EndAngle=3.14159
    g6: LineSegment StartX=121.19 StartY=-3.8 StartZ=0 EndX=121.19 EndY=24.1 EndZ=0
    g7: LineSegment StartX=123.69 StartY=-3.8 StartZ=0 EndX=123.69 EndY=24.1 EndZ=0
    g8: LineSegment StartX=125.2 StartY=43.4 StartZ=0 EndX=125.2 EndY=39.4 EndZ=0
    g9: LineSegment StartX=125.2 StartY=39.4 StartZ=0 EndX=122.7 EndY=39.4 EndZ=0
    g10: LineSegment StartX=122.7 StartY=39.4 StartZ=0 EndX=122.7 EndY=43.4 EndZ=0
    g11: LineSegment StartX=122.7 StartY=43.4 StartZ=0 EndX=125.2 EndY=43.4 EndZ=0
    g12: ArcOfCircle CenterX=107.2 CenterY=32.9 CenterZ=0 NormalX=0 NormalY=0 NormalZ=1 AngleXU=0 Radius=1.25 StartAngle=3.14159 EndAngle=6.28319
    g13: ArcOfCircle CenterX=107.2 CenterY=37.9 CenterZ=0 NormalX=0 NormalY=0 NormalZ=1 AngleXU=0 Radius=1.25 StartAngle=1.5e-15 EndAngle=3.14159
    g14: LineSegment StartX=105.95 StartY=32.9 StartZ=0 EndX=105.95 EndY=37.9 EndZ=0
    g15: LineSegment StartX=108.45 StartY=32.9 StartZ=0 EndX=108.45 EndY=37.9 EndZ=0
    g16: ArcOfCircle CenterX=121.7 CenterY=37.9 CenterZ=0 NormalX=0 NormalY=0 NormalZ=1 AngleXU=0 Radius=1.25 StartAngle=0 EndAngle=2.85184
    g17: ArcOfCircle CenterX=121.7 CenterY=32.9 CenterZ=0 NormalX=0 NormalY=0 NormalZ=1 AngleXU=0 Radius=1.25 StartAngle=3.43134 EndAngle=6.28319
    g18: LineSegment StartX=122.95 StartY=37.9 StartZ=0 EndX=122.95 EndY=32.9 EndZ=0
    g19: ArcOfCircle CenterX=109.039 CenterY=41.168 CenterZ=0 NormalX=0 NormalY=0 NormalZ=1 AngleXU=0 Radius=1 StartAngle=2.35619 EndAngle=5.49779
    g20: ArcOfCircle CenterX=120.961 CenterY=53.0896 CenterZ=0 NormalX=0 NormalY=0 NormalZ=1 AngleXU=0 Radius=1 StartAngle=5.49779 EndAngle=8.63938
    g21: LineSegment StartX=108.332 StartY=41.8751 StartZ=0 EndX=120.254 EndY=53.7967 EndZ=0
    g22: LineSegment StartX=109.746 StartY=40.4609 StartZ=0 EndX=121.668 EndY=52.3825 EndZ=0
    g23: ArcOfCircle CenterX=110.95 CenterY=38.1291 CenterZ=0 NormalX=0 NormalY=0 NormalZ=1 AngleXU=0 Radius=1 StartAngle=2.35619 EndAngle=5.49779
    g24: ArcOfCircle CenterX=122.8 CenterY=49.9791 CenterZ=0 NormalX=0 NormalY=0 NormalZ=1 AngleXU=0 Radius=1 StartAngle=5.49779 EndAngle=8.63938
    g25: LineSegment StartX=110.243 StartY=38.8362 StartZ=0 EndX=122.093 EndY=50.6862 EndZ=0
    g26: LineSegment StartX=111.657 StartY=37.422 StartZ=0 EndX=123.507 EndY=49.272 EndZ=0
    g27: LineSegment StartX=120.023 StartY=32.9 StartZ=0 EndX=118.2 EndY=32.9 EndZ=0
    g28: LineSegment StartX=117.7 StartY=33.4 StartZ=0 EndX=117.7 EndY=37.4 EndZ=0
    g29: LineSegment StartX=118.2 StartY=37.9 StartZ=0 EndX=120.023 EndY=37.9 EndZ=0
    g30: ArcOfCircle CenterX=118.2 CenterY=37.4 CenterZ=0 NormalX=0 NormalY=0 NormalZ=1 AngleXU=0 Radius=0.5 StartAngle=1.5708 EndAngle=3.14159
    g31: GeomPoint X=117.7 Y=37.9 Z=0
    g32: ArcOfCircle CenterX=118.2 CenterY=33.4 CenterZ=0 NormalX=0 NormalY=0 NormalZ=1 AngleXU=0 Radius=0.5 StartAngle=3.14159 EndAngle=4.71239
    g33: ArcOfCircle CenterX=120.023 CenterY=32.4 CenterZ=0 NormalX=0 NormalY=0 NormalZ=1 AngleXU=0 Radius=0.5 StartAngle=0.289752 EndAngle=1.5708
    g34: ArcOfCircle CenterX=120.023 CenterY=38.4 CenterZ=0 NormalX=0 NormalY=0 NormalZ=1 AngleXU=0 Radius=0.5 StartAngle=4.71239 EndAngle=5.99343
    g35: GeomPoint X=117.7 Y=35.4 Z=0
    g36: GeomPoint X=122.95 Y=35.4 Z=0
    g37: ArcOfCircle CenterX=118.171 CenterY=40.4 CenterZ=0 NormalX=0 NormalY=0 NormalZ=1 AngleXU=0 Radius=1 StartAngle=2.35619 EndAngle=5.49779
    g38: ArcOfCircle CenterX=122.8 CenterY=45.0293 CenterZ=0 NormalX=0 NormalY=0 NormalZ=1 AngleXU=0 Radius=1 StartAngle=5.49779 EndAngle=8.63938
    g39: LineSegment StartX=117.464 StartY=41.1071 StartZ=0 EndX=122.093 EndY=45.7364 EndZ=0
    g40: LineSegment StartX=118.878 StartY=39.6929 StartZ=0 EndX=123.507 EndY=44.3222 EndZ=0
    g41: ArcOfCircle CenterX=110.94 CenterY=33.1696 CenterZ=0 NormalX=0 NormalY=0 NormalZ=1 AngleXU=0 Radius=1 StartAngle=2.35619 EndAngle=5.49779
    g42: ArcOfCircle CenterX=115.2 CenterY=37.4293 CenterZ=0 NormalX=0 NormalY=0 NormalZ=1 AngleXU=0 Radius=1 StartAngle=5.49779 EndAngle=8.63938
    g43: LineSegment StartX=110.233 StartY=33.8767 StartZ=0 EndX=114.493 EndY=38.1365 EndZ=0
    g44: LineSegment StartX=111.647 StartY=32.4625 StartZ=0 EndX=115.907 EndY=36.7222 EndZ=0
    g45: ArcOfCircle CenterX=109.655 CenterY=26.9346 CenterZ=0 NormalX=0 NormalY=0 NormalZ=1 AngleXU=0 Radius=1 StartAngle=2.35619 EndAngle=5.49779
    g46: ArcOfCircle CenterX=115.311 CenterY=32.5908 CenterZ=0 NormalX=0 NormalY=0 NormalZ=1 AngleXU=0 Radius=1 StartAngle=5.49779 EndAngle=8.63938
    g47: LineSegment StartX=108.948 StartY=27.6418 StartZ=0 EndX=114.604 EndY=33.2979 EndZ=0
    g48: LineSegment StartX=110.362 StartY=26.2275 StartZ=0 EndX=116.018 EndY=31.8837 EndZ=0
    g49: ArcOfCircle CenterX=110.95 CenterY=23.2799 CenterZ=0 NormalX=0 NormalY=0 NormalZ=1 AngleXU=0 Radius=1 StartAngle=2.35619 EndAngle=5.49779
    g50: ArcOfCircle CenterX=118.07 CenterY=30.4 CenterZ=0 NormalX=0 NormalY=0 NormalZ=1 AngleXU=0 Radius=1 StartAngle=5.49779 EndAngle=8.63938
    g51: LineSegment StartX=110.243 StartY=23.987 StartZ=0 EndX=117.363 EndY=31.1071 EndZ=0
    g52: LineSegment StartX=111.657 StartY=22.5727 StartZ=0 EndX=118.777 EndY=29.6929 EndZ=0
    g53: ArcOfCircle CenterX=110.95 CenterY=18.3301 CenterZ=0 NormalX=0 NormalY=0 NormalZ=1 AngleXU=0 Radius=1 StartAngle=2.35619 EndAngle=5.49779
    g54: ArcOfCircle CenterX=121.771 CenterY=29.1507 CenterZ=0 NormalX=0 NormalY=0 NormalZ=1 AngleXU=0 Radius=1 StartAngle=5.49779 EndAngle=8.63938
    g55: LineSegment StartX=110.243 StartY=19.0372 StartZ=0 EndX=121.063 EndY=29.8578 EndZ=0
    g56: LineSegment StartX=111.657 StartY=17.623 StartZ=0 EndX=122.478 EndY=28.4436 EndZ=0
    g57: ArcOfCircle CenterX=110.95 CenterY=13.3804 CenterZ=0 NormalX=0 NormalY=0 NormalZ=1 AngleXU=0 Radius=1 StartAngle=2.35619 EndAngle=5.49779
    g58: ArcOfCircle CenterX=118.69 CenterY=21.1204 CenterZ=0 NormalX=0 NormalY=0 NormalZ=1 AngleXU=0 Radius=1 StartAngle=5.49779 EndAngle=8.63938
    g59: LineSegment StartX=110.243 StartY=14.0875 StartZ=0 EndX=117.983 EndY=21.8275 EndZ=0
    g60: LineSegment StartX=111.657 StartY=12.6733 StartZ=0 EndX=119.397 EndY=20.4132 EndZ=0
    g61: ArcOfCircle CenterX=110.95 CenterY=8.43061 CenterZ=0 NormalX=0 NormalY=0 NormalZ=1 AngleXU=0 Radius=1 StartAngle=2.35619 EndAngle=5.49779
    g62: ArcOfCircle CenterX=118.69 CenterY=16.1706 CenterZ=0 NormalX=0 NormalY=0 NormalZ=1 AngleXU=0 Radius=1 StartAngle=5.49779 EndAngle=8.63938
    g63: LineSegment StartX=110.243 StartY=9.13772 StartZ=0 EndX=117.983 EndY=16.8777 EndZ=0
    g64: LineSegment StartX=111.657 StartY=7.7235 StartZ=0 EndX=119.397 EndY=15.4635 EndZ=0
    g65: ArcOfCircle CenterX=110.95 CenterY=3.48086 CenterZ=0 NormalX=0 NormalY=0 NormalZ=1 AngleXU=0 Radius=1 StartAngle=2.35619 EndAngle=5.49779
    g66: ArcOfCircle CenterX=118.69 CenterY=11.2209 CenterZ=0 NormalX=0 NormalY=0 NormalZ=1 AngleXU=0 Radius=1 StartAngle=5.49779 EndAngle=8.63938
    g67: LineSegment StartX=110.243 StartY=4.18797 StartZ=0 EndX=117.983 EndY=11.928 EndZ=0
    g68: LineSegment StartX=111.657 StartY=2.77376 StartZ=0 EndX=119.397 EndY=10.5138 EndZ=0
    g69: ArcOfCircle CenterX=110.95 CenterY=-1.46888 CenterZ=0 NormalX=0 NormalY=0 NormalZ=1 AngleXU=0 Radius=1 StartAngle=2.35619 EndAngle=5.49779
    g70: ArcOfCircle CenterX=118.69 CenterY=6.27112 CenterZ=0 NormalX=0 NormalY=0 NormalZ=1 AngleXU=0 Radius=1 StartAngle=5.49779 EndAngle=8.63938
    g71: LineSegment StartX=110.243 StartY=-0.761775 StartZ=0 EndX=117.983 EndY=6.97822 EndZ=0
    g72: LineSegment StartX=111.657 StartY=-2.17599 StartZ=0 EndX=119.397 EndY=5.56401 EndZ=0
    g73: ArcOfCircle CenterX=110.469 CenterY=-6.9 CenterZ=0 NormalX=0 NormalY=0 NormalZ=1 AngleXU=0 Radius=1 StartAngle=2.35619 EndAngle=5.49779
    g74: ArcOfCircle CenterX=118.69 CenterY=1.32137 CenterZ=0 NormalX=0 NormalY=0 NormalZ=1 AngleXU=0 Radius=1 StartAngle=5.49779 EndAngle=8.63938
    g75: LineSegment StartX=109.762 StartY=-6.19289 StartZ=0 EndX=117.983 EndY=2.02848 EndZ=0
    g76: LineSegment StartX=111.176 StartY=-7.60711 StartZ=0 EndX=119.397 EndY=0.614262 EndZ=0
    g77: ArcOfCircle CenterX=115.418 CenterY=-6.9 CenterZ=0 NormalX=0 NormalY=0 NormalZ=1 AngleXU=0 Radius=1 StartAngle=2.35619 EndAngle=5.49779
    g78: ArcOfCircle CenterX=118.69 CenterY=-3.62838 CenterZ=0 NormalX=0 NormalY=0 NormalZ=1 AngleXU=0 Radius=1 StartAngle=5.49779 EndAngle=8.63938
    g79: LineSegment StartX=114.711 StartY=-6.19289 StartZ=0 EndX=117.983 EndY=-2.92127 EndZ=0
    g80: LineSegment StartX=116.125 StartY=-7.60711 StartZ=0 EndX=119.397 EndY=-4.33548 EndZ=0
    g81: ArcOfCircle CenterX=120.368 CenterY=-6.9 CenterZ=0 NormalX=0 NormalY=0 NormalZ=1 AngleXU=0 Radius=1 StartAngle=2.35619 EndAngle=5.49779
    g82: ArcOfCircle CenterX=120.425 CenterY=-6.84329 CenterZ=0 NormalX=0 NormalY=0 NormalZ=1 AngleXU=0 Radius=1 StartAngle=5.49779 EndAngle=8.63938
    g83: LineSegment StartX=119.661 StartY=-6.19289 StartZ=0 EndX=119.718 EndY=-6.13618 EndZ=0
    g84: LineSegment StartX=121.075 StartY=-7.60711 StartZ=0 EndX=121.132 EndY=-7.5504 EndZ=0
    g85: ArcOfCircle CenterX=84.1455 CenterY=21.316 CenterZ=0 NormalX=0 NormalY=0 NormalZ=1 AngleXU=0 Radius=1 StartAngle=2.35619 EndAngle=5.49779
    g86: ArcOfCircle CenterX=88.8122 CenterY=25.9826 CenterZ=0 NormalX=0 NormalY=0 NormalZ=1 AngleXU=0 Radius=1 StartAngle=5.49779 EndAngle=8.63938
    g87: LineSegment StartX=83.4384 StartY=22.0231 StartZ=0 EndX=88.1051 EndY=26.6898 EndZ=0
    g88: LineSegment StartX=84.8526 StartY=20.6089 StartZ=0 EndX=89.5193 EndY=25.2755 EndZ=0
  constraints (222):
    c: Tangent(g0,g2) = 1.5708
    c: Tangent(g0,g3) = -1.5708
    c: Tangent(g1,g2) = 1.5708
    c: Tangent(g1,g3) = -1.5708
    c: Equal(g0,g1)
    c: Vertical(g3)
    c: Radius(g0) = 1.25
    c: DistanceX(g-1,g0) = 107.2
    c: DistanceY(g0,g-1) = 3.8
    c: DistanceY(g0,g1) = 27.9
    c: Tangent(g4,g6) = 1.5708
    c: Tangent(g4,g7) = -1.5708
    c: Tangent(g5,g6) = 1.5708
    c: Tangent(g5,g7) = -1.5708
    c: Equal(g4,g5)
    c: Vertical(g7)
    c: Radius(g4) = 1.25
    c: DistanceX(g0,g4) = 15.24
    c: Horizontal(g4,g0)
    c: Horizontal(g5,g1)
    c: Coincident(g8,g9)
    c: Coincident(g9,g10)
    c: Coincident(g10,g11)
    c: Coincident(g11,g8)
    c: Vertical(g8)
    c: Vertical(g10)
    c: Horizontal(g9)
    c: Horizontal(g11)
    c: Distance(g5,g11) = 19.3
    c: Distance(g9,g9) = 2.5
    c: Distance(g-3,g8) = 0.1
    c: DistanceY(g10,g10) = 4
    c: Tangent(g12,g14) = 1.5708
    c: Tangent(g12,g15) = -1.5708
    c: Tangent(g13,g14) = 1.5708
    c: Tangent(g13,g15) = -1.5708
    c: Equal(g12,g13)
    c: Radius(g12) = 1.25
    c: Vertical(g14)
    c: Vertical(g12,g1)
    c: DistanceY(g1,g12) = 8.8
    c: DistanceY(g12,g13) = 5
    c: Tangent(g16,g18) = 1.5708
    c: Tangent(g17,g18) = 1.5708
    c: Equal(g16,g17)
    c: Radius(g16) = 1.25
    c: Horizontal(g17,g12)
    c: Horizontal(g16,g13)
    c: DistanceX(g12,g17) = 14.5
    c: Tangent(g19,g21) = 1.5708
    c: Tangent(g19,g22) = -1.5708
    c: Tangent(g20,g21) = 1.5708
    c: Tangent(g20,g22) = -1.5708
    c: Equal(g19,g20)
    c: Angle(g-1,g21) = 0.785398
    c: Radius(g19) = 1
    c: Distance(g-5,g21) = 1.5
    c: Distance(g19,g13) = 1.5
    c: Distance(g20,g-4) = 1.5
    c: Tangent(g23,g25) = 1.5708
    c: Tangent(g23,g26) = -1.5708
    c: Tangent(g24,g25) = 1.5708
    c: Tangent(g24,g26) = -1.5708
    c: Equal(g23,g24)
    c: Angle(g-1,g25) = 0.785398
    c: Radius(g23) = 1
    c: Distance(g22,g25) = 1.5
    c: Distance(g23,g15) = 1.5
    c: Distance(g24,g-3) = 1.5
    c: Horizontal(g29)
    c: Horizontal(g27)
    c: Vertical(g18)
    c: PointOnObject(g31,g28)
    c: PointOnObject(g31,g29)
    c: Tangent(g28,g30) = 1.5708
    c: Tangent(g29,g30) = 1.5708
    c: Tangent(g28,g32) = 1.5708
    c: Tangent(g27,g32) = 1.5708
    c: Equal(g32,g30)
    c: Vertical(g28)
    c: Tangent(g27,g33) = -1.5708
    c: Tangent(g17,g33) = 1.5708
    c: Tangent(g29,g34) = -1.5708
    c: Tangent(g16,g34) = 1.5708
    c: Equal(g34,g33)
    c: Equal(g33,g30)
    c: Radius(g30) = 0.5
    c: Distance(g17,g28) = 4
    c: Distance(g27,g29) = 5
    c: Symmetric(g28,g28,g35)
    c: Symmetric(g18,g18,g36)
    c: Horizontal(g35,g36)
    c: Tangent(g37,g39) = 1.5708
    c: Tangent(g37,g40) = -1.5708
    c: Tangent(g38,g39) = 1.5708
    c: Tangent(g38,g40) = -1.5708
    c: Equal(g37,g38)
    c: Angle(g-1,g39) = 0.785398
    c: Radius(g37) = 1
    c: Distance(g26,g39) = 1.5
    c: Distance(g38,g-3) = 1.5
    c: Distance(g37,g29) = 1.5
    c: Tangent(g41,g43) = 1.5708
    c: Tangent(g41,g44) = -1.5708
    c: Tangent(g42,g43) = 1.5708
    c: Tangent(g42,g44) = -1.5708
    c: Equal(g41,g42)
    c: Angle(g-1,g43) = 0.785398
    c: Radius(g41) = 1
    c: Tangent(g45,g47) = 1.5708
    c: Tangent(g45,g48) = -1.5708
    c: Tangent(g46,g47) = 1.5708
    c: Tangent(g46,g48) = -1.5708
    c: Equal(g45,g46)
    c: Angle(g-1,g47) = 0.785398
    c: Radius(g45) = 1
    c: Tangent(g49,g51) = 1.5708
    c: Tangent(g49,g52) = -1.5708
    c: Tangent(g50,g51) = 1.5708
    c: Tangent(g50,g52) = -1.5708
    c: Equal(g49,g50)
    c: Angle(g-1,g51) = 0.785398
    c: Radius(g49) = 1
    c: Tangent(g53,g55) = 1.5708
    c: Tangent(g53,g56) = -1.5708
    c: Tangent(g54,g55) = 1.5708
    c: Tangent(g54,g56) = -1.5708
    c: Equal(g53,g54)
    c: Angle(g-1,g55) = 0.785398
    c: Radius(g53) = 1
    c: Distance(g26,g43) = 1.5
    c: Distance(g44,g47) = 1.5
    c: Distance(g51,g48) = 1.5
    c: Distance(g55,g52) = 1.5
    c: Tangent(g57,g59) = 1.5708
    c: Tangent(g57,g60) = -1.5708
    c: Tangent(g58,g59) = 1.5708
    c: Tangent(g58,g60) = -1.5708
    c: Equal(g57,g58)
    c: Angle(g-1,g59) = 0.785398
    c: Radius(g57) = 1
    c: Tangent(g61,g63) = 1.5708
    c: Tangent(g61,g64) = -1.5708
    c: Tangent(g62,g63) = 1.5708
    c: Tangent(g62,g64) = -1.5708
    c: Equal(g61,g62)
    c: Angle(g-1,g63) = 0.785398
    c: Radius(g61) = 1
    c: Tangent(g65,g67) = 1.5708
    c: Tangent(g65,g68) = -1.5708
    c: Tangent(g66,g67) = 1.5708
    c: Tangent(g66,g68) = -1.5708
    c: Equal(g65,g66)
    c: Angle(g-1,g67) = 0.785398
    c: Radius(g65) = 1
    c: Distance(g59,g56) = 1.5
    c: Distance(g63,g60) = 1.5
    c: Distance(g45,g1) = 1.5
    c: Distance(g41,g12) = 1.5
    c: Distance(g42,g28) = 1.5
    c: Distance(g46,g32) = 1.5
    c: Distance(g49,g3) = 1.5
    c: Distance(g50,g27) = 1.5
    c: Distance(g54,g17) = 1.5
    c: Distance(g53,g3) = 1.5
    c: Distance(g58,g6) = 1.5
    c: Distance(g57,g3) = 1.5
    c: Distance(g62,g6) = 1.5
    c: Distance(g61,g3) = 1.5
    c: Distance(g64,g67) = 1.5
    c: Distance(g66,g6) = 1.5
    c: Distance(g65,g3) = 1.5
    c: Tangent(g69,g71) = 1.5708
    c: Tangent(g69,g72) = -1.5708
    c: Tangent(g70,g71) = 1.5708
    c: Tangent(g70,g72) = -1.5708
    c: Equal(g69,g70)
    c: Angle(g-1,g71) = 0.785398
    c: Radius(g69) = 1
    c: Distance(g68,g71) = 1.5
    c: Distance(g70,g6) = 1.5
    c: Distance(g69,g3) = 1.5
    c: Tangent(g73,g75) = 1.5708
    c: Tangent(g73,g76) = -1.5708
    c: Tangent(g74,g75) = 1.5708
    c: Tangent(g74,g76) = -1.5708
    c: Equal(g73,g74)
    c: Angle(g-1,g75) = 0.785398
    c: Radius(g73) = 1
    c: Distance(g72,g75) = 1.5
    c: Distance(g74,g6) = 1.5
    c: Distance(g73,g-6) = 1.5
    c: Tangent(g77,g79) = 1.5708
    c: Tangent(g77,g80) = -1.5708
    c: Tangent(g78,g79) = 1.5708
    c: Tangent(g78,g80) = -1.5708
    c: Equal(g77,g78)
    c: Angle(g-1,g79) = 0.785398
    c: Radius(g77) = 1
    c: Distance(g76,g79) = 1.5
    c: Distance(g78,g6) = 1.5
    c: Distance(g77,g-6) = 1.5
    c: Tangent(g81,g83) = 1.5708
    c: Tangent(g81,g84) = -1.5708
    c: Tangent(g82,g83) = 1.5708
    c: Tangent(g82,g84) = -1.5708
    c: Equal(g81,g82)
    c: Angle(g-1,g83) = 0.785398
    c: Radius(g81) = 1
    c: Distance(g80,g83) = 1.5
    c: Distance(g81,g-6) = 1.5
    c: Distance(g82,g4) = 1.4
    c: Tangent(g85,g87) = 1.5708
    c: Tangent(g85,g88) = -1.5708
    c: Tangent(g86,g87) = 1.5708
    c: Tangent(g86,g88) = -1.5708
    c: Equal(g85,g86)
    c: Angle(g-1,g87) = 0.785398
    c: Radius(g85) = 1
    c: Distance(g-7,g88) = 1.5
    c: Distance(g86,g-8) = 1.5
    c: Horizontal(g85,g-7)
FEATURE [PartDesign::Pocket] Pocket003
  BaseFeature = -> Pocket002
  Direction = (0,0,1)
  Length = 5
  Length2 = 5
  Profile = -> Sketch007
  ReferenceAxis = -> Sketch007 [N_Axis]
  Suppressed = false
  Type = 1
FEATURE [PartDesign::Pad] Pad003
  BaseFeature = -> Pocket003
  Direction = (0,0,-1)
  Length = 10
  Length2 = 10
  Profile = -> Sketch004
  ReferenceAxis = -> Sketch004 [N_Axis]
  Reversed = true
  Suppressed = false
  Type = 3
  UpToFace = -> Pocket003 [Face4]
FEATURE [Sketcher::SketchObject] Sketch008
  AttachmentSupport = -> [Pad003]
  ExternalGeometry = -> [Pad003]
  FullyConstrained = true
  MapMode = 5
  Placement = pos=(0,0,-1.6) rot=(1,0,0;3.14159rad)
  sketch-geometry (5):
    g0: Circle CenterX=9.5 CenterY=28.5 CenterZ=0 NormalX=0 NormalY=0 NormalZ=1 AngleXU=0 Radius=1.05
    g1: Circle CenterX=9.5 CenterY=9.5 CenterZ=0 NormalX=0 NormalY=0 NormalZ=1 AngleXU=0 Radius=1.05
    g2: Circle CenterX=85.5 CenterY=5.5 CenterZ=0 NormalX=0 NormalY=0 NormalZ=1 AngleXU=0 Radius=1.05
    g3: Circle CenterX=56.5 CenterY=42.9 CenterZ=0 NormalX=0 NormalY=0 NormalZ=1 AngleXU=0 Radius=1.05
    g4: Circle CenterX=101.5 CenterY=47.5 CenterZ=0 NormalX=0 NormalY=0 NormalZ=1 AngleXU=0 Radius=1.05
  constraints (10):
    c: Coincident(g0,g-4)
    c: Coincident(g1,g-3)
    c: Coincident(g2,g-7)
    c: Coincident(g3,g-5)
    c: Coincident(g4,g-6)
    c: Equal(g3,g0)
    c: Equal(g0,g1)
    c: Equal(g1,g2)
    c: Equal(g2,g4)
    c: Diameter(g0) = 2.1
FEATURE [PartDesign::Pocket] Pocket004
  BaseFeature = -> Pad003
  Direction = (0,0,1)
  Length = 5
  Length2 = 5
  Profile = -> Sketch008
  ReferenceAxis = -> Sketch008 [N_Axis]
  Suppressed = false
  Type = 1
FEATURE [PartDesign::Body] Body003
  BaseFeature = -> Cut002
  Group = -> [BaseFeature,DatumPlane,Sketch003,Pocket,LinearPattern,Sketch004,Pad002,Sketch005,Pocket001,LinearPattern001,Sketch006,Pocket002,Sketch007,Pocket003,Pad003,Sketch008,Pocket004]
  Origin = -> Origin003
  Tip = -> Pocket004
COMPONENT P2 — recipe-attached ("cutout001", modeled in this document).
Construction recipe (the document's own serialized feature program — sketch geometry with constraints, then the solid features built on it; lengths are millimeters unless a unit is written):

FEATURE [Sketcher::SketchObject] Sketch  label="smd cutout"
  FullyConstrained = true
  sketch-geometry (67):
    g0: LineSegment StartX=-9.5 StartY=-9.5 StartZ=0 EndX=9.5 EndY=-9.5 EndZ=0
    g1: LineSegment StartX=9.5 StartY=-9.5 StartZ=0 EndX=9.5 EndY=9.5 EndZ=0
    g2: LineSegment StartX=9.5 StartY=9.5 StartZ=0 EndX=-9.5 EndY=9.5 EndZ=0
    g3: LineSegment StartX=-9.5 StartY=9.5 StartZ=0 EndX=-9.5 EndY=-9.5 EndZ=0
    g4: Circle CenterX=-3.81 CenterY=2.54 CenterZ=0 NormalX=0 NormalY=0 NormalZ=1 AngleXU=0 Radius=1.5
    g5: Circle CenterX=2.54 CenterY=5.08 CenterZ=0 NormalX=0 NormalY=0 NormalZ=1 AngleXU=0 Radius=1.5
    g6: Circle CenterX=0 CenterY=0 CenterZ=0 NormalX=0 NormalY=0 NormalZ=1 AngleXU=0 Radius=2
    g7: Circle CenterX=5 CenterY=0 CenterZ=0 NormalX=0 NormalY=0 NormalZ=1 AngleXU=0 Radius=1
    g8: Circle CenterX=-5 CenterY=0 CenterZ=0 NormalX=0 NormalY=0 NormalZ=1 AngleXU=0 Radius=1
    g9: GeomPoint X=-8.5 Y=1 Z=0
    g10: GeomPoint X=-8.5 Y=4 Z=0
    g11: GeomPoint X=-6 Y=4 Z=0
    g12: GeomPoint X=-2.5 Y=1 Z=0
    g13: GeomPoint X=-0.4 Y=2.9 Z=0
    g14: GeomPoint X=4.5 Y=2.9 Z=0
    g15: GeomPoint X=4.5 Y=3.6 Z=0
    g16: GeomPoint X=7.1 Y=6.7 Z=0
    g17: GeomPoint X=-4 Y=6.7 Z=0
    g18: LineSegment StartX=-8.5 StartY=1 StartZ=0 EndX=-2.5 EndY=1 EndZ=0
    g19: LineSegment StartX=-8.5 StartY=1 StartZ=0 EndX=-8.5 EndY=4 EndZ=0
    g20: LineSegment StartX=-8.5 StartY=4 StartZ=0 EndX=-6 EndY=4 EndZ=0
    g21: LineSegment StartX=-6 StartY=4 StartZ=0 EndX=-6 EndY=4.7 EndZ=0
    g22: LineSegment StartX=-4 StartY=6.7 StartZ=0 EndX=7.1 EndY=6.7 EndZ=0
    g23: LineSegment StartX=7.1 StartY=6.7 StartZ=0 EndX=7.1 EndY=3.6 EndZ=0
    g24: LineSegment StartX=7.1 StartY=3.6 StartZ=0 EndX=4.5 EndY=3.6 EndZ=0
    g25: LineSegment StartX=4.5 StartY=2.9 StartZ=0 EndX=4.5 EndY=3.6 EndZ=0
    g26: LineSegment StartX=4.5 StartY=2.9 StartZ=0 EndX=-0.4 EndY=2.9 EndZ=0
    g27: ArcOfCircle CenterX=-0.4 CenterY=0.789474 CenterZ=0 NormalX=0 NormalY=0 NormalZ=1 AngleXU=0 Radius=2.11053 StartAngle=1.5708 EndAngle=3.04168
    g28: LineSegment StartX=6.85 StartY=2.35 StartZ=0 EndX=6.85 EndY=-2.35 EndZ=0
    g29: LineSegment StartX=6.85 StartY=-2.35 StartZ=0 EndX=9.15 EndY=-2.35 EndZ=0
    g30: LineSegment StartX=9.15 StartY=-2.35 StartZ=0 EndX=9.15 EndY=2.35 EndZ=0
    g31: ArcOfCircle CenterX=-4 CenterY=4.7 CenterZ=0 NormalX=0 NormalY=0 NormalZ=1 AngleXU=0 Radius=2 StartAngle=1.5708 EndAngle=3.14159
    g32: LineSegment StartX=6.85 StartY=2.35 StartZ=0 EndX=9.15 EndY=2.35 EndZ=0
    g33: LineSegment StartX=-8.8 StartY=0.8 StartZ=0 EndX=-8.8 EndY=4.2 EndZ=0
    g34: LineSegment StartX=-8.3 StartY=4.7 StartZ=0 EndX=-7.1607 EndY=4.7 EndZ=0
    g35: LineSegment StartX=-4 StartY=7.4 StartZ=0 EndX=7.3 EndY=7.4 EndZ=0
    g36: LineSegment StartX=7.8 StartY=6.9 StartZ=0 EndX=7.8 EndY=3.55 EndZ=0
    g37: LineSegment StartX=9.5 StartY=2.55 StartZ=0 EndX=9.5 EndY=-2.55 EndZ=0
    g38: LineSegment StartX=9 StartY=-3.05 StartZ=0 EndX=6.65 EndY=-3.05 EndZ=0
    g39: LineSegment StartX=-8.3 StartY=0.3 StartZ=0 EndX=-7.19089 EndY=0.3 EndZ=0
    g40: ArcOfCircle CenterX=-5 CenterY=0 CenterZ=0 NormalX=0 NormalY=0 NormalZ=1 AngleXU=0 Radius=1.7 StartAngle=3.23263 EndAngle=4.71239
    g41: ArcOfCircle CenterX=0 CenterY=0 CenterZ=0 NormalX=0 NormalY=0 NormalZ=1 AngleXU=0 Radius=2.7 StartAngle=3.89963 EndAngle=5.52514
    g42: LineSegment StartX=-5 StartY=-1.7 StartZ=0 EndX=-2.32379 EndY=-1.7 EndZ=0
    g43: LineSegment StartX=6.15 StartY=-2.55 StartZ=0 EndX=6.15 EndY=-2.2 EndZ=0
    g44: LineSegment StartX=2.32379 StartY=-1.7 StartZ=0 EndX=5.65 EndY=-1.7 EndZ=0
    g45: ArcOfCircle CenterX=-4 CenterY=4.7 CenterZ=0 NormalX=0 NormalY=0 NormalZ=1 AngleXU=0 Radius=2.7 StartAngle=1.5708 EndAngle=2.9847
    g46: ArcOfCircle CenterX=-2.32379 CenterY=-2.2 CenterZ=0 NormalX=0 NormalY=0 NormalZ=1 AngleXU=0 Radius=0.5 StartAngle=0.758041 EndAngle=1.5708
    g47: ArcOfCircle CenterX=2.32379 CenterY=-2.2 CenterZ=0 NormalX=0 NormalY=0 NormalZ=1 AngleXU=0 Radius=0.5 StartAngle=1.5708 EndAngle=2.38355
    g48: ArcOfCircle CenterX=5.65 CenterY=-2.2 CenterZ=0 NormalX=0 NormalY=0 NormalZ=1 AngleXU=0 Radius=0.5 StartAngle=0 EndAngle=1.5708
    g49: GeomPoint X=6.15 Y=-1.7 Z=0
    g50: ArcOfCircle CenterX=6.65 CenterY=-2.55 CenterZ=0 NormalX=0 NormalY=0 NormalZ=1 AngleXU=0 Radius=0.5 StartAngle=3.14159 EndAngle=4.71239
    g51: GeomPoint X=6.15 Y=-3.05 Z=0
    g52: ArcOfCircle CenterX=9 CenterY=-2.55 CenterZ=0 NormalX=0 NormalY=0 NormalZ=1 AngleXU=0 Radius=0.5 StartAngle=4.71239 EndAngle=6.28319
    g53: GeomPoint X=9.5 Y=-3.05 Z=0
    g54: LineSegment StartX=8.3 StartY=3.05 StartZ=0 EndX=9 EndY=3.05 EndZ=0
    g55: ArcOfCircle CenterX=9 CenterY=2.55 CenterZ=0 NormalX=0 NormalY=0 NormalZ=1 AngleXU=0 Radius=0.5 StartAngle=3e-16 EndAngle=1.5708
    g56: GeomPoint X=9.5 Y=3.05 Z=0
    g57: ArcOfCircle CenterX=8.3 CenterY=3.55 CenterZ=0 NormalX=0 NormalY=0 NormalZ=1 AngleXU=0 Radius=0.5 StartAngle=3.14159 EndAngle=4.71239
    g58: GeomPoint X=7.8 Y=3.05 Z=0
    g59: ArcOfCircle CenterX=7.3 CenterY=6.9 CenterZ=0 NormalX=0 NormalY=0 NormalZ=1 AngleXU=0 Radius=0.5 StartAngle=-9e-16 EndAngle=1.5708
    g60: GeomPoint X=7.8 Y=7.4 Z=0
    g61: ArcOfCircle CenterX=-7.1607 CenterY=5.2 CenterZ=0 NormalX=0 NormalY=0 NormalZ=1 AngleXU=0 Radius=0.5 StartAngle=4.71239 EndAngle=6.12629
    g62: ArcOfCircle CenterX=-8.3 CenterY=4.2 CenterZ=0 NormalX=0 NormalY=0 NormalZ=1 AngleXU=0 Radius=0.5 StartAngle=1.5708 EndAngle=3.14159
    g63: GeomPoint X=-8.8 Y=4.7 Z=0
    g64: ArcOfCircle CenterX=-8.3 CenterY=0.8 CenterZ=0 NormalX=0 NormalY=0 NormalZ=1 AngleXU=0 Radius=0.5 StartAngle=3.14159 EndAngle=4.71239
    g65: GeomPoint X=-8.8 Y=0.3 Z=0
    g66: ArcOfCircle CenterX=-7.19089 CenterY=-0.2 CenterZ=0 NormalX=0 NormalY=0 NormalZ=1 AngleXU=0 Radius=0.5 StartAngle=0.0910348 EndAngle=1.5708
  constraints (157):
    c: Coincident(g2,g3)
    c: Horizontal(g0)
    c: Horizontal(g2)
    c: Vertical(g1)
    c: PointOnObject(g7,g-1)
    c: Equal(g4,g5)
    c: Symmetric(g7,g8,g-2)
    c: Equal(g8,g7)
    c: DistanceX(g-1,g5) = 2.54
    c: Distance(g5,g-1) = 5.08
    c: DistanceX(g2,g2) = 19
    c: Equal(g2,g3)
    c: Distance(g4,g-2) = 3.81
    c: Distance(g4,g-1) = 2.54
    c: Distance(g8,g-2) = 5
    c: Distance(g9,g-1) = 1
    c: Coincident(g18,g9)
    c: Coincident(g18,g12)
    c: Horizontal(g18)
    c: Distance(g9,g-2) = 8.5
    c: Coincident(g19,g9)
    c: Coincident(g19,g10)
    c: Vertical(g19)
    c: Distance(g10,g-1) = 4
    c: Coincident(g20,g10)
    c: Coincident(g20,g11)
    c: Horizontal(g20)
    c: Distance(g11,g-2) = 6
    c: Distance(g17,g-2) = 4
    c: DistanceY(g-1,g17) = 6.7
    c: Coincident(g21,g11)
    c: Vertical(g21)
    c: Coincident(g22,g17)
    c: Coincident(g22,g16)
    c: Horizontal(g22)
    c: DistanceX(g-1,g16) = 7.1
    c: Coincident(g23,g16)
    c: Vertical(g23)
    c: Distance(g23,g-1) = 3.6
    c: Coincident(g24,g23)
    c: Coincident(g24,g15)
    c: Coincident(g25,g14)
    c: Coincident(g25,g15)
    c: Coincident(g26,g14)
    c: Coincident(g26,g13)
    c: Horizontal(g24)
    c: Horizontal(g26)
    c: Vertical(g25)
    c: Distance(g-2,g25) = 4.5
    c: Distance(g14,g-1) = 2.9
    c: Distance(g13,g-2) = 0.4
    c: Distance(g12,g-2) = 2.5
    c: Coincident(g27,g13)
    c: Coincident(g27,g12)
    c: Diameter(g5) = 3
    c: Diameter(g8) = 2
    c: Diameter(g6) = 4
    c: Vertical(g30)
    c: Horizontal(g29)
    c: Distance(g28,g-2) = 6.85
    c: Distance(g28,g-1) = 2.35
    c: Symmetric(g28,g28,g-1)
    c: Vertical(g3)
    c: Coincident(g31,g17)
    c: Tangent(g31,g21) = 1.5708
    c: Coincident(g32,g28)
    c: Coincident(g32,g30)
    c: Horizontal(g32)
    c: Coincident(g6,g-1)
    c: Symmetric(g0,g1,g6)
    c: Coincident(g3,g0)
    c: Coincident(g2,g1)
    c: Coincident(g1,g0)
    c: DistanceX(g29,g29) = 2.3
    c: Coincident(g29,g30)
    c: Coincident(g29,g28)
    c: Tangent(g27,g26)
    c: Tangent(g31,g22)
    c: Vertical(g33)
    c: Horizontal(g34)
    c: Horizontal(g35)
    c: Vertical(g36)
    c: PointOnObject(g56,g1)
    c: PointOnObject(g53,g1)
    c: Horizontal(g38)
    c: Horizontal(g39)
    c: Distance(g20,g34) = 0.7
    c: Distance(g65,g19) = 0.3
    c: Distance(g18,g39) = 0.7
    c: Coincident(g40,g8)
    c: Coincident(g41,g6)
    c: Horizontal(g42)
    c: Vertical(g43)
    c: Tangent(g44,g42)
    c: Distance(g28,g43) = 0.7
    c: Distance(g53,g29) = 0.7
    c: Tangent(g42,g40) = -1.5708
    c: Distance(g23,g36) = 0.7
    c: Distance(g35,g22) = 0.7
    c: Coincident(g45,g31)
    c: Tangent(g45,g35) = 1.5708
    c: Tangent(g42,g46) = 1.5708
    c: Tangent(g41,g46) = 1.5708
    c: Tangent(g41,g47) = 1.5708
    c: Tangent(g44,g47) = 1.5708
    c: PointOnObject(g49,g44)
    c: PointOnObject(g49,g43)
    c: Tangent(g44,g48) = 1.5708
    c: Tangent(g43,g48) = -1.5708
    c: PointOnObject(g51,g43)
    c: PointOnObject(g51,g38)
    c: Tangent(g43,g50) = 1.5708
    c: Tangent(g38,g50) = 1.5708
    c: PointOnObject(g53,g38)
    c: PointOnObject(g53,g37)
    c: Tangent(g38,g52) = 1.5708
    c: Tangent(g37,g52) = 1.5708
    c: Horizontal(g54)
    c: Distance(g32,g54) = 0.7
    c: PointOnObject(g56,g37)
    c: PointOnObject(g56,g54)
    c: Tangent(g37,g55) = 1.5708
    c: Tangent(g54,g55) = 1.5708
    c: PointOnObject(g58,g54)
    c: PointOnObject(g58,g36)
    c: Tangent(g54,g57) = -1.5708
    c: Tangent(g36,g57) = -1.5708
    c: PointOnObject(g60,g35)
    c: PointOnObject(g60,g36)
    c: Tangent(g35,g59) = 1.5708
    c: Tangent(g36,g59) = 1.5708
    c: Tangent(g34,g61) = -1.5708
    c: Tangent(g45,g61) = 1.5708
    c: PointOnObject(g63,g34)
    c: PointOnObject(g63,g33)
    c: Tangent(g34,g62) = 1.5708
    c: Tangent(g33,g62) = 1.5708
    c: PointOnObject(g65,g39)
    c: PointOnObject(g65,g33)
    c: Tangent(g39,g64) = -1.5708
    c: Tangent(g33,g64) = 1.5708
    c: Tangent(g40,g66) = 1.5708
    c: Tangent(g39,g66) = 1.5708
    c: Radius(g46) = 0.5
    c: Equal(g66,g64)
    c: Equal(g64,g46)
    c: Equal(g46,g47)
    c: Equal(g47,g48)
    c: Equal(g48,g50)
    c: Equal(g50,g57)
    c: Equal(g57,g59)
    c: Equal(g59,g61)
    c: Equal(g61,g62)
    c: Equal(g57,g55)
    c: Equal(g52,g50)
    c: Distance(g40,g8) = 0.7
    c: Distance(g41,g6) = 0.7
FEATURE [PartDesign::Pad] Pad001
  Direction = (0,0,1)
  Length = 1.5
  Length2 = 10
  Profile = -> Sketch
  ReferenceAxis = -> Sketch [N_Axis]
  Suppressed = false
  Type = 0
  expr: Length = <<constants>>.base_normal
FEATURE [PartDesign::Body] Body001  label="cutout"
  Group = -> [Sketch,Pad001]
  Origin = -> Origin001
  Tip = -> Pad001
COMPONENT P3 — same part as P2; its construction recipe is shown at P2.
PROVENANCE & LICENSES
A FreeCAD (.FCStd) document from a public repository crawl; recipes are the document's own serialized feature recipes (and, for linked parts, companion documents' recipes).
License: as declared in the source repository (recorded in the dataset sidecar).
